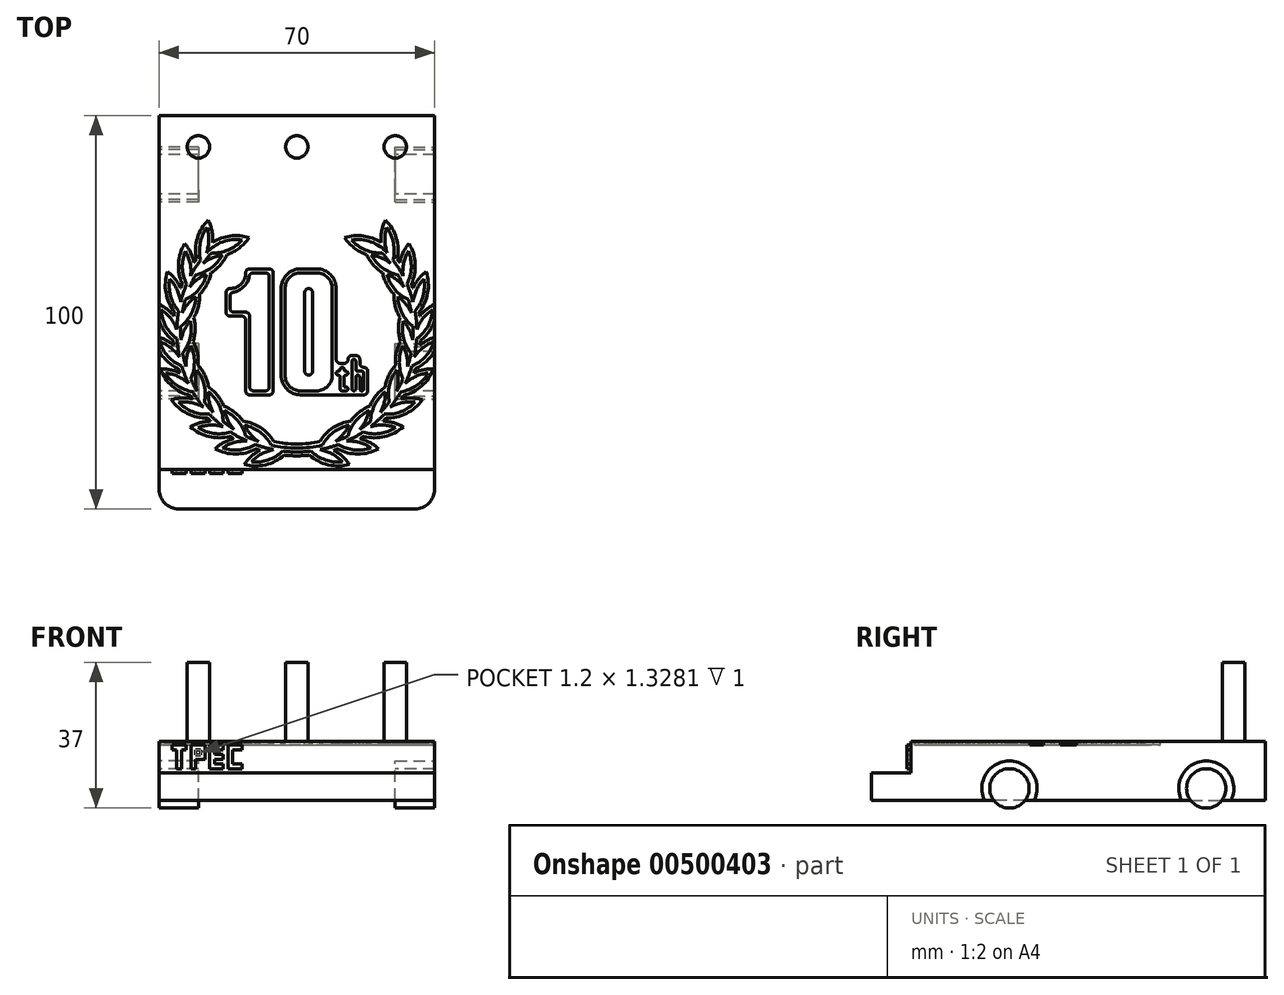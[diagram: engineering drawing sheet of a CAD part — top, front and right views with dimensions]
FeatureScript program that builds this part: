
annotation { "Feature Type Name" : "Feature", "Feature Type Description" : "" }
export const myFeature = defineFeature(function(context is Context, id is Id, definition is map)
    precondition{}
    {
        {
            var Q0;
            Q0=qCreatedBy(makeId("Top.planeOp"),FACE);
            var sketch = newSketch(context, id + "F0", { "sketchPlane" : qUnion([Q0])});
            skLineSegment(sketch, "E0.bottom", {"start": v(35, -50) * mm, "end": v(-35, -50) * mm});
            skLineSegment(sketch, "E0.top", {"start": v(35, 50) * mm, "end": v(-35, 50) * mm});
            skLineSegment(sketch, "E0.left", {"start": v(35, -50) * mm, "end": v(35, 50) * mm});
            skLineSegment(sketch, "E0.right", {"start": v(-35, -50) * mm, "end": v(-35, 50) * mm});
            skPoint(sketch, "E0.middle", {"position": v(0, 0) * mm});
            skSolve(sketch);
        }
        {
            var Q0;
            Q0 = qSketchRegion(id + "F0", true);
            extrude(context, id + "F1", {"entities" : qUnion([Q0]), "depth" : 15 * mm});
        }
        {
            var Q0;
            Q0=makeQuery(id+"F1.opExtrude","CAP_FACE",FACE,{"disambiguationData":[OSD([sQuery(id+"F0.wireOp",EDGE,"E0.bottom"),sQuery(id+"F0.wireOp",EDGE,"E0.top"),sQuery(id+"F0.wireOp",EDGE,"E0.left"),sQuery(id+"F0.wireOp",EDGE,"E0.right")])],"isStart":false});
            var sketch = newSketch(context, id + "F2", { "sketchPlane" : qUnion([Q0])});
            skLineSegment(sketch, "E1.bottom", {"start": v(35, -50) * mm, "end": v(-35, -50) * mm});
            skLineSegment(sketch, "E1.top", {"start": v(35, -40) * mm, "end": v(-35, -40) * mm});
            skLineSegment(sketch, "E1.left", {"start": v(35, -50) * mm, "end": v(35, -40) * mm});
            skLineSegment(sketch, "E1.right", {"start": v(-35, -50) * mm, "end": v(-35, -40) * mm});
            skSolve(sketch);
        }
        {
            var Q0;
            Q0 = qSketchRegion(id + "F2", true);
            extrude(context, id + "F3", {"entities" : qUnion([Q0]), "operationType" : NewBodyOperationType.REMOVE, "oppositeDirection" : true, "depth" : 8 * mm});
        }
        {
            var Q0;
            Q0=makeQuery(id+"F1.opExtrude","CAP_FACE",FACE,{"disambiguationData":[OSD([sQuery(id+"F0.wireOp",EDGE,"E0.bottom"),sQuery(id+"F0.wireOp",EDGE,"E0.top"),sQuery(id+"F0.wireOp",EDGE,"E0.left"),sQuery(id+"F0.wireOp",EDGE,"E0.right")])],"isStart":false});
            var sketch = newSketch(context, id + "F4", { "sketchPlane" : qUnion([Q0])});
            skLineSegment(sketch, "E2", {"start": v(-65.6, 42) * mm, "end": v(65.6, 42) * mm, "construction": true});
            skLineSegment(sketch, "E3", {"start": v(0, 50) * mm, "end": v(0, -40) * mm, "construction": true});
            skCircle(sketch, "E4", {"center": v(0, 42) * mm, "radius": 2.85 * mm});
            skCircle(sketch, "E5", {"center": v(-25, 42) * mm, "radius": 2.85 * mm});
            skCircle(sketch, "E6.MirrorC", {"center": v(25, 42) * mm, "radius": 2.85 * mm});
            skSolve(sketch);
        }
        {
            var Q0;
            Q0 = qSketchRegion(id + "F4", true);
            extrude(context, id + "F5", {"entities" : qUnion([Q0]), "operationType" : NewBodyOperationType.ADD, "depth" : 20 * mm});
        }
        {
            var Q0;
            Q0=makeQuery(id+"F1.opExtrude","SWEPT_FACE",FACE,{"disambiguationData":[OSD([sQuery(id+"F0.wireOp",EDGE,"E0.left")])]});
            var sketch = newSketch(context, id + "F6", { "sketchPlane" : qUnion([Q0])});
            skLineSegment(sketch, "E7", {"start": v(-57.55, -2) * mm, "end": v(59.86, -2) * mm, "construction": true});
            skLineSegment(sketch, "E8", {"start": v(-15, 24.29) * mm, "end": v(-15, -23.36) * mm, "construction": true});
            skLineSegment(sketch, "E9", {"start": v(35, 23.38) * mm, "end": v(35, -24.94) * mm, "construction": true});
            skPoint(sketch, "E10", {"position": v(-15, -2) * mm});
            skPoint(sketch, "E11", {"position": v(35, -2) * mm});
            skLineSegment(sketch, "E12", {"start": v(-54.96, 3) * mm, "end": v(63.1, 3) * mm, "construction": true});
            skPoint(sketch, "E13", {"position": v(-15, 3) * mm});
            skPoint(sketch, "E14", {"position": v(35, 3) * mm});
            skCircle(sketch, "E15", {"center": v(-15, 3) * mm, "radius": 5 * mm, "construction": true});
            skCircle(sketch, "E16", {"center": v(35, 3) * mm, "radius": 5 * mm, "construction": true});
            skLineSegment(sketch, "E17.bottom", {"start": v(-21, 0) * mm, "end": v(-9, 0) * mm});
            skLineSegment(sketch, "E17.top", {"start": v(-21, 9) * mm, "end": v(-9, 9) * mm});
            skLineSegment(sketch, "E17.left", {"start": v(-21, 0) * mm, "end": v(-21, 9) * mm});
            skLineSegment(sketch, "E17.right", {"start": v(-9, 0) * mm, "end": v(-9, 9) * mm});
            skLineSegment(sketch, "E18.bottom", {"start": v(29, 0) * mm, "end": v(41, 0) * mm});
            skLineSegment(sketch, "E18.top", {"start": v(29, 9) * mm, "end": v(41, 9) * mm});
            skLineSegment(sketch, "E18.left", {"start": v(29, 0) * mm, "end": v(29, 9) * mm});
            skLineSegment(sketch, "E18.right", {"start": v(41, 0) * mm, "end": v(41, 9) * mm});
            skPoint(sketch, "E19", {"position": v(-15, 9) * mm});
            skPoint(sketch, "E20", {"position": v(35, 9) * mm});
            skSolve(sketch);
        }
        {
            var Q0;
            Q0=qCreatedBy(makeId("Right.planeOp"),FACE);
            var sketch = newSketch(context, id + "F7", { "sketchPlane" : qUnion([Q0])});
            skLineSegment(sketch, "E21.0", {"start": v(-54.96, 3) * mm, "end": v(63.1, 3) * mm, "construction": true});
            skPoint(sketch, "E22.0", {"position": v(-15, 3) * mm});
            skPoint(sketch, "E23.0", {"position": v(35, 3) * mm});
            skCircle(sketch, "E24.0", {"center": v(-15, 3) * mm, "radius": 5 * mm});
            skCircle(sketch, "E24.1", {"center": v(35, 3) * mm, "radius": 5 * mm});
            skSolve(sketch);
        }
        {
            var Q0;
            Q0 = qSketchRegion(id + "F7", true);
            var Q1;
            Q1=makeQuery(id+"F1.opExtrude","SWEPT_FACE",FACE,{"disambiguationData":[OSD([sQuery(id+"F0.wireOp",EDGE,"E0.left")])]});
            var Q2;
            Q2=makeQuery(id+"F1.opExtrude","SWEPT_FACE",FACE,{"disambiguationData":[OSD([sQuery(id+"F0.wireOp",EDGE,"E0.right")])]});
            extrude(context, id + "F8", {"entities" : qUnion([Q0]), "operationType" : NewBodyOperationType.ADD, "endBound" : BoundingType.UP_TO_SURFACE, "endBoundEntityFace" : qUnion([Q1]), "depth" : 25 * mm, "hasSecondDirection" : true, "secondDirectionBound" : SecondDirectionBoundingType.UP_TO_SURFACE, "secondDirectionOppositeDirection" : true, "secondDirectionBoundEntityFace" : qUnion([Q2]), "secondDirectionDepth" : 25 * mm});
        }
        {
            var Q0;
            Q0=qCreatedBy(makeId("Right.planeOp"),FACE);
            var sketch = newSketch(context, id + "F9", { "sketchPlane" : qUnion([Q0])});
            skArc(sketch, "E25.0", {"start": v(-19, 0) * mm, "mid": v(-15, -2) * mm, "end": v(-11, 0) * mm});
            skArc(sketch, "E26.0", {"start": v(31, 0) * mm, "mid": v(35, -2) * mm, "end": v(39, 0) * mm});
            skLineSegment(sketch, "E27.0", {"start": v(-11, 0) * mm, "end": v(31, 0) * mm, "construction": true});
            skLineSegment(sketch, "E28", {"start": v(-11, 0) * mm, "end": v(-19, 0) * mm});
            skLineSegment(sketch, "E29", {"start": v(31, 0) * mm, "end": v(39, 0) * mm});
            skSolve(sketch);
        }
        {
            var Q0;
            Q0 = qSketchRegion(id + "F9", true);
            extrude(context, id + "F10", {"entities" : qUnion([Q0]), "operationType" : NewBodyOperationType.REMOVE, "oppositeDirection" : true, "depth" : 25 * mm, "hasSecondDirection" : true, "secondDirectionOppositeDirection" : false, "secondDirectionDepth" : 25 * mm});
        }
        {
            var Q0;
            Q0=makeQuery(id+"F6.imprint","IMPRINT",FACE,{"disambiguationData":[TD([[makeQuery(id+"F6.imprint","IMPRINT",EDGE,{"derivedFrom":sQuery(id+"F6.wireOp",EDGE,"E17.top")}),1.0]])]});
            var sketch = newSketch(context, id + "F11", { "sketchPlane" : qUnion([Q0])});
            skCircle(sketch, "E30.0", {"center": v(-15, 3) * mm, "radius": 5 * mm});
            skCircle(sketch, "E31.0", {"center": v(-15, 3) * mm, "radius": 7 * mm});
            skCircle(sketch, "E32.0", {"center": v(35, 3) * mm, "radius": 5 * mm});
            skCircle(sketch, "E33.0", {"center": v(35, 3) * mm, "radius": 7 * mm});
            skSolve(sketch);
        }
        {
            var Q0;
            Q0 = qSketchRegion(id + "F11", true);
            extrude(context, id + "F12", {"entities" : qUnion([Q0]), "operationType" : NewBodyOperationType.REMOVE, "oppositeDirection" : true, "depth" : 10 * mm});
        }
        {
            var Q0;
            Q0=makeQuery(id+"F8.boolean.opBoolean","MERGE",FACE,{"derivedFrom":[makeQuery(id+"F1.opExtrude","SWEPT_FACE",FACE,{"disambiguationData":[OSD([sQuery(id+"F0.wireOp",EDGE,"E0.right")])]}),makeQuery(id+"F8.opExtrude","CAP_FACE",FACE,{"disambiguationData":[OSD([sQuery(id+"F7.wireOp",EDGE,"E24.0")])],"isStart":true}),makeQuery(id+"F8.opExtrude","CAP_FACE",FACE,{"disambiguationData":[OSD([sQuery(id+"F7.wireOp",EDGE,"E24.1")])],"isStart":true})]});
            var sketch = newSketch(context, id + "F13", { "sketchPlane" : qUnion([Q0])});
            skCircle(sketch, "E34.0", {"center": v(15, 3) * mm, "radius": 5 * mm});
            skCircle(sketch, "E34.1", {"center": v(-35, 3) * mm, "radius": 5 * mm});
            skCircle(sketch, "E35.0", {"center": v(15, 3) * mm, "radius": 7 * mm});
            skCircle(sketch, "E36.0", {"center": v(-35, 3) * mm, "radius": 7 * mm});
            skSolve(sketch);
        }
        {
            var Q0;
            Q0 = qSketchRegion(id + "F13", true);
            extrude(context, id + "F14", {"entities" : qUnion([Q0]), "operationType" : NewBodyOperationType.REMOVE, "oppositeDirection" : true, "depth" : 10 * mm});
        }
        {
            var Q0;
            Q0=makeQuery(id+"F1.opExtrude","SWEPT_EDGE",EDGE,{"disambiguationData":[OSD([sQuery(id+"F0.wireOp",EDGE,"E0.bottom"),sQuery(id+"F0.wireOp",EDGE,"E0.left")])]});
            var Q1;
            Q1=makeQuery(id+"F1.opExtrude","SWEPT_EDGE",EDGE,{"disambiguationData":[OSD([sQuery(id+"F0.wireOp",EDGE,"E0.bottom"),sQuery(id+"F0.wireOp",EDGE,"E0.right")])]});
            fillet(context, id + "F15", {"entities" : qUnion([Q0, Q1]), "radius" : 5 * mm, "tangentPropagation" : true, "allowEdgeOverflow" : false});
        }
        {
            var Q0;
            Q0=makeQuery(id+"F3.boolean.opBoolean","COPY",FACE,{"derivedFrom":makeQuery(id+"F3.opExtrude","SWEPT_FACE",FACE,{"disambiguationData":[OSD([sQuery(id+"F2.wireOp",EDGE,"E1.top")])]})});
            var sketch = newSketch(context, id + "F16", { "sketchPlane" : qUnion([Q0])});
            skLineSegment(sketch, "E37", {"start": v(-31.71, 14) * mm, "end": v(-28.11, 14) * mm});
            skLineSegment(sketch, "E38", {"start": v(-28.11, 14) * mm, "end": v(-28.11, 12.8) * mm});
            skLineSegment(sketch, "E39", {"start": v(-28.11, 12.8) * mm, "end": v(-29.31, 12.8) * mm});
            skLineSegment(sketch, "E40", {"start": v(-29.31, 12.8) * mm, "end": v(-29.31, 8) * mm});
            skLineSegment(sketch, "E41", {"start": v(-29.31, 8) * mm, "end": v(-30.51, 8) * mm});
            skLineSegment(sketch, "E42", {"start": v(-30.51, 8) * mm, "end": v(-30.51, 12.8) * mm});
            skLineSegment(sketch, "E43", {"start": v(-30.51, 12.8) * mm, "end": v(-31.71, 12.8) * mm});
            skLineSegment(sketch, "E44", {"start": v(-31.71, 12.8) * mm, "end": v(-31.71, 14) * mm});
            skLineSegment(sketch, "E45", {"start": v(-26.91, 14) * mm, "end": v(-26.91, 8) * mm});
            skLineSegment(sketch, "E46", {"start": v(-26.91, 8) * mm, "end": v(-25.71, 8) * mm});
            skLineSegment(sketch, "E47", {"start": v(-25.71, 8) * mm, "end": v(-25.71, 10.4) * mm});
            skLineSegment(sketch, "E48", {"start": v(-25.71, 10.4) * mm, "end": v(-23.31, 10.4) * mm});
            skLineSegment(sketch, "E49", {"start": v(-23.31, 10.4) * mm, "end": v(-23.31, 14) * mm});
            skLineSegment(sketch, "E50", {"start": v(-23.31, 14) * mm, "end": v(-26.91, 14) * mm});
            skLineSegment(sketch, "E51", {"start": v(-22.11, 14) * mm, "end": v(-22.11, 8) * mm});
            skLineSegment(sketch, "E52", {"start": v(-22.11, 8) * mm, "end": v(-18.67, 8) * mm});
            skLineSegment(sketch, "E53", {"start": v(-18.67, 8) * mm, "end": v(-18.67, 9.2) * mm});
            skLineSegment(sketch, "E54", {"start": v(-18.67, 9.2) * mm, "end": v(-20.91, 9.2) * mm});
            skLineSegment(sketch, "E55", {"start": v(-20.91, 9.2) * mm, "end": v(-20.91, 10.4) * mm});
            skLineSegment(sketch, "E56", {"start": v(-20.91, 10.4) * mm, "end": v(-18.67, 10.4) * mm});
            skLineSegment(sketch, "E57", {"start": v(-18.67, 10.4) * mm, "end": v(-18.67, 11.6) * mm});
            skLineSegment(sketch, "E58", {"start": v(-18.67, 11.6) * mm, "end": v(-20.91, 11.6) * mm});
            skLineSegment(sketch, "E59", {"start": v(-20.91, 11.6) * mm, "end": v(-20.91, 12.8) * mm});
            skLineSegment(sketch, "E60", {"start": v(-20.91, 12.8) * mm, "end": v(-18.67, 12.8) * mm});
            skLineSegment(sketch, "E61", {"start": v(-18.67, 12.8) * mm, "end": v(-18.67, 14) * mm});
            skLineSegment(sketch, "E62", {"start": v(-18.67, 14) * mm, "end": v(-22.11, 14) * mm});
            skLineSegment(sketch, "E63", {"start": v(-13.87, 14) * mm, "end": v(-17.47, 14) * mm});
            skLineSegment(sketch, "E64", {"start": v(-17.47, 14) * mm, "end": v(-17.47, 8) * mm});
            skLineSegment(sketch, "E65", {"start": v(-17.47, 8) * mm, "end": v(-13.87, 8) * mm});
            skLineSegment(sketch, "E66", {"start": v(-13.87, 8) * mm, "end": v(-13.87, 9.2) * mm});
            skLineSegment(sketch, "E67", {"start": v(-13.87, 9.2) * mm, "end": v(-16.27, 9.2) * mm});
            skLineSegment(sketch, "E68", {"start": v(-13.87, 14) * mm, "end": v(-13.87, 12.8) * mm});
            skLineSegment(sketch, "E69", {"start": v(-13.87, 12.8) * mm, "end": v(-16.27, 12.8) * mm});
            skLineSegment(sketch, "E70", {"start": v(-16.27, 12.8) * mm, "end": v(-16.27, 9.2) * mm});
            skLineSegment(sketch, "E71.bottom", {"start": v(-25.71, 11.47) * mm, "end": v(-24.51, 11.47) * mm});
            skLineSegment(sketch, "E71.top", {"start": v(-25.71, 12.8) * mm, "end": v(-24.51, 12.8) * mm});
            skLineSegment(sketch, "E71.left", {"start": v(-25.71, 11.47) * mm, "end": v(-25.71, 12.8) * mm});
            skLineSegment(sketch, "E71.right", {"start": v(-24.51, 11.47) * mm, "end": v(-24.51, 12.8) * mm});
            skSolve(sketch);
        }
        {
            var Q0;
            Q0 = qSketchRegion(id + "F16", true);
            extrude(context, id + "F17", {"entities" : qUnion([Q0]), "operationType" : NewBodyOperationType.ADD, "depth" : 1 * mm});
        }
        {
            var Q0;
            Q0=makeQuery(id+"F1.opExtrude","CAP_FACE",FACE,{"disambiguationData":[OSD([sQuery(id+"F0.wireOp",EDGE,"E0.bottom"),sQuery(id+"F0.wireOp",EDGE,"E0.top"),sQuery(id+"F0.wireOp",EDGE,"E0.left"),sQuery(id+"F0.wireOp",EDGE,"E0.right")])],"isStart":false});
            var sketch = newSketch(context, id + "F18", { "sketchPlane" : qUnion([Q0])});
            skLineSegment(sketch, "E72", {"start": v(-35, 30) * mm, "end": v(35, 30) * mm, "construction": true});
            skLineSegment(sketch, "E73", {"start": v(35, 30) * mm, "end": v(35, -40) * mm, "construction": true});
            skLineSegment(sketch, "E74", {"start": v(35, -40) * mm, "end": v(-35, -40) * mm, "construction": true});
            skLineSegment(sketch, "E75", {"start": v(-35, -40) * mm, "end": v(-35, 30) * mm, "construction": true});
            skCircle(sketch, "E76", {"center": v(0, -5) * mm, "radius": 30 * mm, "construction": true});
            skArc(sketch, "E77.0", {"start": v(5.88, -34.93) * mm, "mid": v(8.2, -34.38) * mm, "end": v(10.47, -33.65) * mm});
            skArc(sketch, "E78.0", {"start": v(9.78, -32.83) * mm, "mid": v(11.4, -32.2) * mm, "end": v(12.98, -31.5) * mm});
            skPoint(sketch, "E79.startSnap0", {"position": v(0, 50) * mm});
            skPoint(sketch, "E79.endSnap0", {"position": v(0, -40) * mm});
            skLineSegment(sketch, "E80", {"start": v(0, -5) * mm, "end": v(3.14, -34.84) * mm, "construction": true});
            skLineSegment(sketch, "E81", {"start": v(0, -5) * mm, "end": v(0, -25.77) * mm, "construction": true});
            skArc(sketch, "E82", {"start": v(11.55, -38.02) * mm, "mid": v(8.98, -36) * mm, "end": v(5.88, -34.93) * mm});
            skLineSegment(sketch, "E83", {"start": v(3.14, -34.84) * mm, "end": v(11.55, -38.02) * mm, "construction": true});
            skArc(sketch, "E84.MirrorCS", {"start": v(11.55, -38.02) * mm, "mid": v(7.26, -37.54) * mm, "end": v(3.58, -35.29) * mm});
            skLineSegment(sketch, "E85", {"start": v(0, -5) * mm, "end": v(6.24, -34.34) * mm, "construction": true});
            skArc(sketch, "E86", {"start": v(13.26, -28.71) * mm, "mid": v(9.33, -30.5) * mm, "end": v(6.52, -33.77) * mm});
            skLineSegment(sketch, "E87", {"start": v(13.26, -28.71) * mm, "end": v(6.24, -34.34) * mm, "construction": true});
            skArc(sketch, "E88.MirrorCS", {"start": v(13.26, -28.71) * mm, "mid": v(11.8, -31) * mm, "end": v(9.78, -32.83) * mm});
            skPoint(sketch, "E89.orphan", {"position": v(6.24, -34.34) * mm});
            skPoint(sketch, "E90.orphan", {"position": v(3.14, -34.84) * mm});
            skArc(sketch, "E91.1.0", {"start": v(18.37, -25.02) * mm, "mid": v(14.96, -27.66) * mm, "end": v(12.98, -31.5) * mm});
            skArc(sketch, "E91.1.1", {"start": v(18.37, -25.02) * mm, "mid": v(17.48, -27.59) * mm, "end": v(15.94, -29.82) * mm});
            skArc(sketch, "E91.1.2", {"start": v(18.86, -34.47) * mm, "mid": v(15.88, -33.1) * mm, "end": v(12.63, -32.76) * mm});
            skArc(sketch, "E91.1.3", {"start": v(18.86, -34.47) * mm, "mid": v(14.57, -34.99) * mm, "end": v(10.47, -33.65) * mm});
            skArc(sketch, "E91.2.0", {"start": v(22.49, -20.24) * mm, "mid": v(19.78, -23.6) * mm, "end": v(18.74, -27.78) * mm});
            skArc(sketch, "E91.2.1", {"start": v(22.49, -20.24) * mm, "mid": v(22.22, -22.95) * mm, "end": v(21.23, -25.48) * mm});
            skArc(sketch, "E91.2.2", {"start": v(25.14, -29.33) * mm, "mid": v(21.94, -28.68) * mm, "end": v(18.69, -29.1) * mm});
            skArc(sketch, "E91.2.3", {"start": v(25.14, -29.33) * mm, "mid": v(21.1, -30.82) * mm, "end": v(16.8, -30.46) * mm});
            skArc(sketch, "E91.3.0", {"start": v(25.4, -14.64) * mm, "mid": v(23.54, -18.53) * mm, "end": v(23.49, -22.85) * mm});
            skArc(sketch, "E91.3.1", {"start": v(25.4, -14.64) * mm, "mid": v(25.76, -17.34) * mm, "end": v(25.38, -20.03) * mm});
            skArc(sketch, "E91.3.2", {"start": v(30.08, -22.87) * mm, "mid": v(26.8, -22.98) * mm, "end": v(23.74, -24.14) * mm});
            skArc(sketch, "E91.3.3", {"start": v(30.08, -22.87) * mm, "mid": v(26.48, -25.26) * mm, "end": v(22.21, -25.9) * mm});
            skArc(sketch, "E91.4.0", {"start": v(26.94, -8.53) * mm, "mid": v(26.02, -12.74) * mm, "end": v(26.97, -16.95) * mm});
            skArc(sketch, "E91.4.1", {"start": v(26.94, -8.53) * mm, "mid": v(27.91, -11.06) * mm, "end": v(28.17, -13.77) * mm});
            skArc(sketch, "E91.4.2", {"start": v(33.39, -15.45) * mm, "mid": v(30.23, -16.32) * mm, "end": v(27.52, -18.15) * mm});
            skArc(sketch, "E91.4.3", {"start": v(33.39, -15.45) * mm, "mid": v(30.44, -18.6) * mm, "end": v(26.43, -20.22) * mm});
            skArc(sketch, "E91.5.0", {"start": v(27.02, -2.22) * mm, "mid": v(27.1, -6.53) * mm, "end": v(29, -10.4) * mm});
            skArc(sketch, "E91.5.1", {"start": v(27.02, -2.22) * mm, "mid": v(28.56, -4.46) * mm, "end": v(29.43, -7.04) * mm});
            skArc(sketch, "E91.5.2", {"start": v(34.9, -7.47) * mm, "mid": v(32.02, -9.04) * mm, "end": v(29.81, -11.45) * mm});
            skArc(sketch, "E91.5.3", {"start": v(34.9, -7.47) * mm, "mid": v(32.75, -11.22) * mm, "end": v(29.23, -13.71) * mm});
            skArc(sketch, "E91.6.0", {"start": v(25.65, 3.94) * mm, "mid": v(26.73, -0.24) * mm, "end": v(29.47, -3.57) * mm});
            skArc(sketch, "E91.6.1", {"start": v(25.65, 3.94) * mm, "mid": v(27.66, 2.1) * mm, "end": v(29.1, -0.2) * mm});
            skArc(sketch, "E91.6.2", {"start": v(34.53, 0.64) * mm, "mid": v(32.1, -1.55) * mm, "end": v(30.5, -4.4) * mm});
            skArc(sketch, "E91.6.3", {"start": v(34.53, 0.64) * mm, "mid": v(33.3, -3.5) * mm, "end": v(30.45, -6.74) * mm});
            skArc(sketch, "E91.7.0", {"start": v(22.9, 9.61) * mm, "mid": v(24.91, 5.8) * mm, "end": v(28.34, 3.18) * mm});
            skArc(sketch, "E91.7.1", {"start": v(22.9, 9.61) * mm, "mid": v(25.28, 8.3) * mm, "end": v(27.21, 6.39) * mm});
            skArc(sketch, "E91.7.2", {"start": v(32.3, 8.45) * mm, "mid": v(30.43, 5.76) * mm, "end": v(29.53, 2.61) * mm});
            skArc(sketch, "E91.7.3", {"start": v(32.3, 8.45) * mm, "mid": v(32.06, 4.14) * mm, "end": v(30.03, 0.33) * mm});
            skArc(sketch, "E91.8.0", {"start": v(18.91, 14.5) * mm, "mid": v(21.75, 11.25) * mm, "end": v(25.7, 9.5) * mm});
            skArc(sketch, "E91.8.1", {"start": v(18.91, 14.5) * mm, "mid": v(21.53, 13.77) * mm, "end": v(23.85, 12.36) * mm});
            skArc(sketch, "E91.8.2", {"start": v(28.32, 15.54) * mm, "mid": v(27.13, 12.5) * mm, "end": v(26.98, 9.22) * mm});
            skArc(sketch, "E91.8.3", {"start": v(28.32, 15.54) * mm, "mid": v(29.09, 11.3) * mm, "end": v(28, 7.12) * mm});
            skArc(sketch, "E91.9.0", {"start": v(13.9, 18.34) * mm, "mid": v(17.42, 15.83) * mm, "end": v(21.65, 15.03) * mm});
            skArc(sketch, "E91.9.3", {"start": v(22.82, 21.52) * mm, "mid": v(24.55, 17.56) * mm, "end": v(24.44, 13.24) * mm});
            skLineSegment(sketch, "E91.anchor1", {"start": v(0, -5) * mm, "end": v(4.18, -44.78) * mm, "construction": true});
            skLineSegment(sketch, "E91.anchor2", {"start": v(0, -5) * mm, "end": v(32.36, 18.51) * mm, "construction": true});
            skArc(sketch, "E92.trimOffspring", {"start": v(12.63, -32.76) * mm, "mid": v(14.75, -31.7) * mm, "end": v(16.8, -30.46) * mm});
            skArc(sketch, "E93.trimOffspring", {"start": v(15.94, -29.82) * mm, "mid": v(17.37, -28.84) * mm, "end": v(18.74, -27.78) * mm});
            skArc(sketch, "E94.trimOffspring", {"start": v(18.69, -29.1) * mm, "mid": v(20.51, -27.57) * mm, "end": v(22.21, -25.9) * mm});
            skArc(sketch, "E95.trimOffspring", {"start": v(21.23, -25.48) * mm, "mid": v(22.4, -24.2) * mm, "end": v(23.49, -22.85) * mm});
            skArc(sketch, "E96.trimOffspring", {"start": v(23.74, -24.14) * mm, "mid": v(25.17, -22.23) * mm, "end": v(26.43, -20.22) * mm});
            skArc(sketch, "E97.trimOffspring", {"start": v(25.38, -20.03) * mm, "mid": v(26.22, -18.51) * mm, "end": v(26.97, -16.95) * mm});
            skArc(sketch, "E98.trimOffspring", {"start": v(27.52, -18.15) * mm, "mid": v(28.46, -15.96) * mm, "end": v(29.23, -13.71) * mm});
            skArc(sketch, "E99.trimOffspring", {"start": v(28.17, -13.77) * mm, "mid": v(28.63, -12.1) * mm, "end": v(29, -10.4) * mm});
            skArc(sketch, "E100.trimOffspring", {"start": v(29.81, -11.45) * mm, "mid": v(30.22, -9.1) * mm, "end": v(30.45, -6.74) * mm});
            skArc(sketch, "E101.trimOffspring", {"start": v(29.43, -7.04) * mm, "mid": v(29.5, -5.3) * mm, "end": v(29.47, -3.57) * mm});
            skArc(sketch, "E102.trimOffspring", {"start": v(30.5, -4.4) * mm, "mid": v(30.35, -2.02) * mm, "end": v(30.03, 0.33) * mm});
            skArc(sketch, "E103.trimOffspring", {"start": v(29.1, -0.2) * mm, "mid": v(28.77, 1.5) * mm, "end": v(28.34, 3.18) * mm});
            skArc(sketch, "E104.trimOffspring", {"start": v(29.53, 2.61) * mm, "mid": v(28.85, 4.9) * mm, "end": v(28, 7.12) * mm});
            skArc(sketch, "E105.trimOffspring", {"start": v(23.87, 12.34) * mm, "mid": v(22.8, 13.72) * mm, "end": v(21.65, 15.03) * mm});
            skArc(sketch, "E106.trimOffspring", {"start": v(26.98, 9.22) * mm, "mid": v(25.8, 11.28) * mm, "end": v(24.44, 13.24) * mm});
            skArc(sketch, "E107.trimOffspring", {"start": v(-24.44, 13.24) * mm, "mid": v(-25.8, 11.28) * mm, "end": v(-26.98, 9.22) * mm});
            skArc(sketch, "E108", {"start": v(25.7, 9.5) * mm, "mid": v(26.5, 7.97) * mm, "end": v(27.21, 6.39) * mm});
            skLineSegment(sketch, "E109", {"start": v(0, -5) * mm, "end": v(24.27, 12.63) * mm, "construction": true});
            skArc(sketch, "E110", {"start": v(22.82, 21.52) * mm, "mid": v(22.36, 18.28) * mm, "end": v(22.98, 15.06) * mm});
            skArc(sketch, "E111", {"start": v(22.98, 15.06) * mm, "mid": v(18.86, 17.86) * mm, "end": v(13.9, 18.34) * mm});
            skArc(sketch, "E112.trimOffspring", {"start": v(-21.65, 15.03) * mm, "mid": v(-22.8, 13.73) * mm, "end": v(-23.85, 12.36) * mm});
            skArc(sketch, "E113.MirrorCS", {"start": v(-22.82, 21.52) * mm, "mid": v(-24.55, 17.56) * mm, "end": v(-24.44, 13.24) * mm});
            skArc(sketch, "E114.MirrorCS", {"start": v(-22.82, 21.52) * mm, "mid": v(-22.36, 18.28) * mm, "end": v(-22.98, 15.06) * mm});
            skArc(sketch, "E115.MirrorCS", {"start": v(-22.98, 15.06) * mm, "mid": v(-18.86, 17.86) * mm, "end": v(-13.9, 18.34) * mm});
            skArc(sketch, "E116.MirrorCS", {"start": v(-13.9, 18.34) * mm, "mid": v(-17.42, 15.83) * mm, "end": v(-21.65, 15.03) * mm});
            skArc(sketch, "E117.MirrorCS", {"start": v(-18.91, 14.5) * mm, "mid": v(-21.53, 13.77) * mm, "end": v(-23.85, 12.36) * mm});
            skArc(sketch, "E118.MirrorCS", {"start": v(-18.91, 14.5) * mm, "mid": v(-21.75, 11.25) * mm, "end": v(-25.7, 9.5) * mm});
            skArc(sketch, "E119.MirrorCS", {"start": v(-28.32, 15.54) * mm, "mid": v(-27.13, 12.5) * mm, "end": v(-26.98, 9.22) * mm});
            skArc(sketch, "E120.MirrorCS", {"start": v(-28.32, 15.54) * mm, "mid": v(-29.09, 11.3) * mm, "end": v(-28, 7.12) * mm});
            skArc(sketch, "E121.MirrorCS", {"start": v(-22.9, 9.61) * mm, "mid": v(-25.28, 8.3) * mm, "end": v(-27.21, 6.39) * mm});
            skArc(sketch, "E122.MirrorCS", {"start": v(-22.9, 9.61) * mm, "mid": v(-24.91, 5.8) * mm, "end": v(-28.34, 3.18) * mm});
            skArc(sketch, "E123.MirrorCS", {"start": v(-32.3, 8.45) * mm, "mid": v(-30.43, 5.76) * mm, "end": v(-29.53, 2.61) * mm});
            skArc(sketch, "E124.MirrorCS", {"start": v(-32.3, 8.45) * mm, "mid": v(-32.06, 4.14) * mm, "end": v(-30.03, 0.33) * mm});
            skArc(sketch, "E125.MirrorCS", {"start": v(-25.65, 3.94) * mm, "mid": v(-27.66, 2.1) * mm, "end": v(-29.1, -0.2) * mm});
            skArc(sketch, "E126.MirrorCS", {"start": v(-25.65, 3.94) * mm, "mid": v(-26.73, -0.24) * mm, "end": v(-29.47, -3.57) * mm});
            skArc(sketch, "E127.MirrorCS", {"start": v(-34.53, 0.64) * mm, "mid": v(-32.1, -1.55) * mm, "end": v(-30.5, -4.4) * mm});
            skArc(sketch, "E128.MirrorCS", {"start": v(-34.53, 0.64) * mm, "mid": v(-33.3, -3.5) * mm, "end": v(-30.45, -6.74) * mm});
            skArc(sketch, "E129.MirrorCS", {"start": v(-27.02, -2.22) * mm, "mid": v(-28.56, -4.46) * mm, "end": v(-29.43, -7.04) * mm});
            skArc(sketch, "E130.MirrorCS", {"start": v(-27.02, -2.22) * mm, "mid": v(-27.1, -6.53) * mm, "end": v(-29, -10.4) * mm});
            skArc(sketch, "E131.MirrorCS", {"start": v(-34.9, -7.47) * mm, "mid": v(-32.75, -11.22) * mm, "end": v(-29.23, -13.71) * mm});
            skArc(sketch, "E132.MirrorCS", {"start": v(-34.9, -7.47) * mm, "mid": v(-32.02, -9.04) * mm, "end": v(-29.81, -11.45) * mm});
            skArc(sketch, "E133.MirrorCS", {"start": v(-26.94, -8.53) * mm, "mid": v(-27.91, -11.06) * mm, "end": v(-28.17, -13.77) * mm});
            skArc(sketch, "E134.MirrorCS", {"start": v(-26.94, -8.53) * mm, "mid": v(-26.02, -12.74) * mm, "end": v(-26.97, -16.95) * mm});
            skArc(sketch, "E135.MirrorCS", {"start": v(-25.4, -14.64) * mm, "mid": v(-25.76, -17.34) * mm, "end": v(-25.38, -20.03) * mm});
            skArc(sketch, "E136.MirrorCS", {"start": v(-33.39, -15.45) * mm, "mid": v(-30.44, -18.6) * mm, "end": v(-26.43, -20.22) * mm});
            skArc(sketch, "E137.MirrorCS", {"start": v(-33.39, -15.45) * mm, "mid": v(-30.23, -16.32) * mm, "end": v(-27.52, -18.15) * mm});
            skArc(sketch, "E138.MirrorCS", {"start": v(-25.4, -14.64) * mm, "mid": v(-23.54, -18.53) * mm, "end": v(-23.49, -22.85) * mm});
            skArc(sketch, "E139.MirrorCS", {"start": v(-30.08, -22.87) * mm, "mid": v(-26.8, -22.98) * mm, "end": v(-23.74, -24.14) * mm});
            skArc(sketch, "E140.MirrorCS", {"start": v(-25.14, -29.33) * mm, "mid": v(-21.1, -30.82) * mm, "end": v(-16.8, -30.46) * mm});
            skArc(sketch, "E141.MirrorCS", {"start": v(-25.14, -29.33) * mm, "mid": v(-21.94, -28.68) * mm, "end": v(-18.69, -29.1) * mm});
            skArc(sketch, "E142.MirrorCS", {"start": v(-30.08, -22.87) * mm, "mid": v(-26.48, -25.26) * mm, "end": v(-22.21, -25.9) * mm});
            skArc(sketch, "E143.MirrorCS", {"start": v(-22.49, -20.24) * mm, "mid": v(-22.22, -22.95) * mm, "end": v(-21.23, -25.48) * mm});
            skArc(sketch, "E144.MirrorCS", {"start": v(-22.49, -20.24) * mm, "mid": v(-19.78, -23.6) * mm, "end": v(-18.74, -27.78) * mm});
            skArc(sketch, "E145.MirrorCS", {"start": v(-11.55, -38.02) * mm, "mid": v(-7.26, -37.54) * mm, "end": v(-3.58, -35.29) * mm});
            skArc(sketch, "E146.MirrorCS", {"start": v(-11.55, -38.02) * mm, "mid": v(-8.98, -36) * mm, "end": v(-5.88, -34.93) * mm});
            skArc(sketch, "E147.MirrorCS", {"start": v(-18.86, -34.47) * mm, "mid": v(-14.57, -34.99) * mm, "end": v(-10.47, -33.65) * mm});
            skArc(sketch, "E148.MirrorCS", {"start": v(-18.86, -34.47) * mm, "mid": v(-15.88, -33.1) * mm, "end": v(-12.63, -32.76) * mm});
            skArc(sketch, "E149.MirrorCS", {"start": v(-18.37, -25.02) * mm, "mid": v(-17.48, -27.59) * mm, "end": v(-15.94, -29.82) * mm});
            skArc(sketch, "E150.MirrorCS", {"start": v(-18.37, -25.02) * mm, "mid": v(-14.96, -27.66) * mm, "end": v(-12.98, -31.5) * mm});
            skArc(sketch, "E151.MirrorCS", {"start": v(-13.26, -28.71) * mm, "mid": v(-11.8, -31) * mm, "end": v(-9.78, -32.83) * mm});
            skArc(sketch, "E152.MirrorCS", {"start": v(-13.26, -28.71) * mm, "mid": v(-9.33, -30.5) * mm, "end": v(-6.52, -33.77) * mm});
            skArc(sketch, "E153.trimOffspring", {"start": v(-25.7, 9.5) * mm, "mid": v(-26.5, 7.97) * mm, "end": v(-27.21, 6.39) * mm});
            skArc(sketch, "E154.trimOffspring", {"start": v(-28, 7.12) * mm, "mid": v(-28.85, 4.9) * mm, "end": v(-29.53, 2.61) * mm});
            skArc(sketch, "E155.trimOffspring", {"start": v(-28.34, 3.18) * mm, "mid": v(-28.77, 1.5) * mm, "end": v(-29.1, -0.2) * mm});
            skArc(sketch, "E156.trimOffspring", {"start": v(-30.03, 0.33) * mm, "mid": v(-30.35, -2.02) * mm, "end": v(-30.5, -4.4) * mm});
            skArc(sketch, "E157.trimOffspring", {"start": v(-29.47, -3.57) * mm, "mid": v(-29.5, -5.3) * mm, "end": v(-29.43, -7.04) * mm});
            skArc(sketch, "E158.trimOffspring", {"start": v(-30.45, -6.74) * mm, "mid": v(-30.22, -9.1) * mm, "end": v(-29.81, -11.45) * mm});
            skArc(sketch, "E159.trimOffspring", {"start": v(-29, -10.4) * mm, "mid": v(-28.63, -12.1) * mm, "end": v(-28.17, -13.77) * mm});
            skArc(sketch, "E160.trimOffspring", {"start": v(-29.23, -13.71) * mm, "mid": v(-28.46, -15.96) * mm, "end": v(-27.52, -18.15) * mm});
            skArc(sketch, "E161.trimOffspring", {"start": v(-26.97, -16.95) * mm, "mid": v(-26.22, -18.51) * mm, "end": v(-25.38, -20.03) * mm});
            skArc(sketch, "E162.trimOffspring", {"start": v(-26.43, -20.22) * mm, "mid": v(-25.17, -22.23) * mm, "end": v(-23.74, -24.14) * mm});
            skArc(sketch, "E163.trimOffspring", {"start": v(-23.49, -22.85) * mm, "mid": v(-22.4, -24.2) * mm, "end": v(-21.23, -25.48) * mm});
            skArc(sketch, "E164.trimOffspring", {"start": v(-22.21, -25.9) * mm, "mid": v(-20.51, -27.57) * mm, "end": v(-18.69, -29.1) * mm});
            skArc(sketch, "E165.trimOffspring", {"start": v(-18.74, -27.78) * mm, "mid": v(-17.37, -28.84) * mm, "end": v(-15.94, -29.82) * mm});
            skArc(sketch, "E166.trimOffspring", {"start": v(-16.8, -30.46) * mm, "mid": v(-14.75, -31.7) * mm, "end": v(-12.63, -32.76) * mm});
            skArc(sketch, "E167.trimOffspring", {"start": v(-12.98, -31.5) * mm, "mid": v(-11.4, -32.2) * mm, "end": v(-9.78, -32.83) * mm});
            skArc(sketch, "E168.trimOffspring", {"start": v(-10.47, -33.65) * mm, "mid": v(-8.2, -34.38) * mm, "end": v(-5.88, -34.93) * mm});
            skArc(sketch, "E169.trimOffspring", {"start": v(-6.52, -33.77) * mm, "mid": v(0, -34.5) * mm, "end": v(6.52, -33.77) * mm});
            skArc(sketch, "E170.trimOffspring", {"start": v(-3.58, -35.29) * mm, "mid": v(0, -35.5) * mm, "end": v(3.58, -35.29) * mm});
            skArc(sketch, "E171.0", {"start": v(12.17, 18.95) * mm, "mid": v(14.6, 16.34) * mm, "end": v(17.72, 14.64) * mm});
            skArc(sketch, "E172.0", {"start": v(17.72, 14.64) * mm, "mid": v(19.42, 12.04) * mm, "end": v(21.77, 10.02) * mm});
            skArc(sketch, "E173.0", {"start": v(24.65, 4.6) * mm, "mid": v(25, 1.51) * mm, "end": v(26.2, -1.35) * mm});
            skArc(sketch, "E174.0", {"start": v(26.2, -1.35) * mm, "mid": v(25.83, -4.43) * mm, "end": v(26.34, -7.49) * mm});
            skArc(sketch, "E175.0", {"start": v(26.34, -7.49) * mm, "mid": v(25.27, -10.4) * mm, "end": v(25.05, -13.5) * mm});
            skArc(sketch, "E176.0", {"start": v(25.05, -13.5) * mm, "mid": v(23.34, -16.08) * mm, "end": v(22.42, -19.04) * mm});
            skArc(sketch, "E177.0", {"start": v(22.42, -19.04) * mm, "mid": v(20.16, -21.17) * mm, "end": v(18.58, -23.84) * mm});
            skArc(sketch, "E178.0", {"start": v(18.58, -23.84) * mm, "mid": v(15.88, -25.38) * mm, "end": v(13.73, -27.61) * mm});
            skArc(sketch, "E179.0", {"start": v(13.73, -27.61) * mm, "mid": v(9.2, -29.36) * mm, "end": v(5.87, -32.89) * mm});
            skArc(sketch, "E180.0", {"start": v(-6.3, -32.8) * mm, "mid": v(-0.22, -33.5) * mm, "end": v(5.87, -32.89) * mm});
            skArc(sketch, "E181.0", {"start": v(21.77, 10.02) * mm, "mid": v(22.83, 7.1) * mm, "end": v(24.65, 4.6) * mm});
            skArc(sketch, "E182.0", {"start": v(22.51, 23.41) * mm, "mid": v(21.57, 20.65) * mm, "end": v(21.39, 17.73) * mm});
            skArc(sketch, "E183.trimOffspring", {"start": v(21.39, 17.73) * mm, "mid": v(16.91, 19.36) * mm, "end": v(12.17, 18.95) * mm});
            skArc(sketch, "E184.0", {"start": v(22.51, 23.41) * mm, "mid": v(25.26, 18.82) * mm, "end": v(25.52, 13.47) * mm});
            skArc(sketch, "E185.0", {"start": v(28.46, 17.46) * mm, "mid": v(27, 15.17) * mm, "end": v(26.13, 12.6) * mm});
            skArc(sketch, "E186.0", {"start": v(28.46, 17.46) * mm, "mid": v(30.07, 12.35) * mm, "end": v(29.09, 7.09) * mm});
            skArc(sketch, "E187.0", {"start": v(29.48, 6.1) * mm, "mid": v(29.29, 6.6) * mm, "end": v(29.09, 7.09) * mm});
            skArc(sketch, "E188.0", {"start": v(32.87, 10.29) * mm, "mid": v(30.92, 8.4) * mm, "end": v(29.48, 6.1) * mm});
            skArc(sketch, "E189.0", {"start": v(32.87, 10.29) * mm, "mid": v(33.27, 4.95) * mm, "end": v(31.1, 0.05) * mm});
            skArc(sketch, "E190.trimOffspring", {"start": v(26.13, 12.6) * mm, "mid": v(25.81, 13.06) * mm, "end": v(25.48, 13.52) * mm});
            skArc(sketch, "E191.0", {"start": v(35, 2.06) * mm, "mid": v(32.95, 0.74) * mm, "end": v(31.25, -1) * mm});
            skArc(sketch, "E192.0", {"start": v(35, -2.1) * mm, "mid": v(33.58, -4.94) * mm, "end": v(31.42, -7.25) * mm});
            skArc(sketch, "E193.0", {"start": v(35, -6.39) * mm, "mid": v(33.07, -7.18) * mm, "end": v(31.32, -8.32) * mm});
            skArc(sketch, "E194.0", {"start": v(35, -9.78) * mm, "mid": v(32.9, -12.5) * mm, "end": v(30.05, -14.44) * mm});
            skArc(sketch, "E195.0", {"start": v(35, -14.42) * mm, "mid": v(32.3, -14.6) * mm, "end": v(29.72, -15.45) * mm});
            skArc(sketch, "E196.0", {"start": v(35, -14.42) * mm, "mid": v(31.88, -18.76) * mm, "end": v(27.07, -21.11) * mm});
            skArc(sketch, "E197.0", {"start": v(26.5, -22.02) * mm, "mid": v(26.79, -21.57) * mm, "end": v(27.07, -21.11) * mm});
            skArc(sketch, "E198.0", {"start": v(31.9, -22.24) * mm, "mid": v(29.21, -21.8) * mm, "end": v(26.5, -22.02) * mm});
            skArc(sketch, "E199.0", {"start": v(31.9, -22.24) * mm, "mid": v(27.84, -25.74) * mm, "end": v(22.62, -26.92) * mm});
            skArc(sketch, "E200.0", {"start": v(21.86, -27.68) * mm, "mid": v(22.25, -27.3) * mm, "end": v(22.62, -26.92) * mm});
            skArc(sketch, "E201.0", {"start": v(27.06, -29.13) * mm, "mid": v(24.55, -28.08) * mm, "end": v(21.86, -27.68) * mm});
            skArc(sketch, "E202.0", {"start": v(27.06, -29.13) * mm, "mid": v(22.3, -31.6) * mm, "end": v(16.96, -31.55) * mm});
            skArc(sketch, "E203.trimOffspring", {"start": v(31.25, -1) * mm, "mid": v(31.17, -0.47) * mm, "end": v(31.1, 0.05) * mm});
            skArc(sketch, "E204.trimOffspring", {"start": v(31.32, -8.32) * mm, "mid": v(31.38, -7.79) * mm, "end": v(31.42, -7.25) * mm});
            skArc(sketch, "E205.trimOffspring", {"start": v(29.72, -15.45) * mm, "mid": v(29.89, -14.95) * mm, "end": v(30.05, -14.44) * mm});
            skArc(sketch, "E206.0", {"start": v(20.76, -34.72) * mm, "mid": v(18.57, -33.12) * mm, "end": v(16.05, -32.1) * mm});
            skArc(sketch, "E207.0", {"start": v(20.76, -34.72) * mm, "mid": v(15.57, -36.03) * mm, "end": v(10.38, -34.74) * mm});
            skArc(sketch, "E208.0", {"start": v(9.36, -35.08) * mm, "mid": v(9.87, -34.91) * mm, "end": v(10.38, -34.74) * mm});
            skArc(sketch, "E209.0", {"start": v(13.35, -38.7) * mm, "mid": v(8, -38.79) * mm, "end": v(3.24, -36.33) * mm});
            skArc(sketch, "E210.0", {"start": v(-3.7, -36.28) * mm, "mid": v(-0.23, -36.5) * mm, "end": v(3.24, -36.33) * mm});
            skArc(sketch, "E211.trimOffspring", {"start": v(16.05, -32.1) * mm, "mid": v(16.5, -31.83) * mm, "end": v(16.96, -31.55) * mm});
            skArc(sketch, "E212.0", {"start": v(13.35, -38.7) * mm, "mid": v(11.58, -36.64) * mm, "end": v(9.36, -35.08) * mm});
            skArc(sketch, "E213.MirrorCS", {"start": v(-22.51, 23.41) * mm, "mid": v(-21.57, 20.65) * mm, "end": v(-21.39, 17.73) * mm});
            skArc(sketch, "E214.MirrorCS", {"start": v(-22.51, 23.41) * mm, "mid": v(-25.26, 18.82) * mm, "end": v(-25.52, 13.47) * mm});
            skArc(sketch, "E215.MirrorCS", {"start": v(-28.46, 17.46) * mm, "mid": v(-27, 15.17) * mm, "end": v(-26.13, 12.6) * mm});
            skArc(sketch, "E216.MirrorCS", {"start": v(-26.13, 12.6) * mm, "mid": v(-25.81, 13.06) * mm, "end": v(-25.48, 13.52) * mm});
            skArc(sketch, "E217.MirrorCS", {"start": v(-28.46, 17.46) * mm, "mid": v(-30.07, 12.35) * mm, "end": v(-29.09, 7.09) * mm});
            skArc(sketch, "E218.MirrorCS", {"start": v(-32.87, 10.29) * mm, "mid": v(-30.92, 8.4) * mm, "end": v(-29.48, 6.1) * mm});
            skArc(sketch, "E219.MirrorCS", {"start": v(-29.48, 6.1) * mm, "mid": v(-29.29, 6.6) * mm, "end": v(-29.09, 7.09) * mm});
            skArc(sketch, "E220.MirrorCS", {"start": v(-32.87, 10.29) * mm, "mid": v(-33.27, 4.95) * mm, "end": v(-31.1, 0.05) * mm});
            skArc(sketch, "E221.MirrorCS", {"start": v(-31.25, -1) * mm, "mid": v(-31.17, -0.47) * mm, "end": v(-31.1, 0.05) * mm});
            skArc(sketch, "E222.MirrorCS", {"start": v(-35, 2.06) * mm, "mid": v(-32.95, 0.74) * mm, "end": v(-31.25, -1) * mm});
            skArc(sketch, "E223.MirrorCS", {"start": v(-35, -6.39) * mm, "mid": v(-33.07, -7.18) * mm, "end": v(-31.32, -8.32) * mm});
            skArc(sketch, "E224.MirrorCS", {"start": v(-35, -2.1) * mm, "mid": v(-33.58, -4.94) * mm, "end": v(-31.42, -7.25) * mm});
            skArc(sketch, "E225.MirrorCS", {"start": v(-31.32, -8.32) * mm, "mid": v(-31.38, -7.79) * mm, "end": v(-31.42, -7.25) * mm});
            skArc(sketch, "E226.MirrorCS", {"start": v(-35, -14.42) * mm, "mid": v(-32.3, -14.6) * mm, "end": v(-29.72, -15.45) * mm});
            skArc(sketch, "E227.MirrorCS", {"start": v(-35, -9.78) * mm, "mid": v(-32.9, -12.5) * mm, "end": v(-30.05, -14.44) * mm});
            skArc(sketch, "E228.MirrorCS", {"start": v(-29.72, -15.45) * mm, "mid": v(-29.89, -14.95) * mm, "end": v(-30.05, -14.44) * mm});
            skArc(sketch, "E229.MirrorCS", {"start": v(-31.9, -22.24) * mm, "mid": v(-29.21, -21.8) * mm, "end": v(-26.5, -22.02) * mm});
            skArc(sketch, "E230.MirrorCS", {"start": v(-35, -14.42) * mm, "mid": v(-31.88, -18.76) * mm, "end": v(-27.07, -21.11) * mm});
            skArc(sketch, "E231.MirrorCS", {"start": v(-26.5, -22.02) * mm, "mid": v(-26.79, -21.57) * mm, "end": v(-27.07, -21.11) * mm});
            skArc(sketch, "E232.MirrorCS", {"start": v(-31.9, -22.24) * mm, "mid": v(-27.84, -25.74) * mm, "end": v(-22.62, -26.92) * mm});
            skArc(sketch, "E233.MirrorCS", {"start": v(-27.06, -29.13) * mm, "mid": v(-24.55, -28.08) * mm, "end": v(-21.86, -27.68) * mm});
            skArc(sketch, "E234.MirrorCS", {"start": v(-21.86, -27.68) * mm, "mid": v(-22.25, -27.3) * mm, "end": v(-22.62, -26.92) * mm});
            skArc(sketch, "E235.MirrorCS", {"start": v(-27.06, -29.13) * mm, "mid": v(-22.3, -31.6) * mm, "end": v(-16.96, -31.55) * mm});
            skArc(sketch, "E236.MirrorCS", {"start": v(-20.76, -34.72) * mm, "mid": v(-18.57, -33.12) * mm, "end": v(-16.05, -32.1) * mm});
            skArc(sketch, "E237.MirrorCS", {"start": v(-16.05, -32.1) * mm, "mid": v(-16.5, -31.83) * mm, "end": v(-16.96, -31.55) * mm});
            skArc(sketch, "E238.MirrorCS", {"start": v(-20.76, -34.72) * mm, "mid": v(-15.57, -36.03) * mm, "end": v(-10.38, -34.74) * mm});
            skArc(sketch, "E239.MirrorCS", {"start": v(-9.36, -35.08) * mm, "mid": v(-9.87, -34.91) * mm, "end": v(-10.38, -34.74) * mm});
            skArc(sketch, "E240.MirrorCS", {"start": v(-13.35, -38.7) * mm, "mid": v(-11.58, -36.64) * mm, "end": v(-9.36, -35.08) * mm});
            skArc(sketch, "E241.MirrorCS", {"start": v(-13.35, -38.7) * mm, "mid": v(-8, -38.79) * mm, "end": v(-3.24, -36.33) * mm});
            skArc(sketch, "E242.MirrorCS", {"start": v(-13.73, -27.61) * mm, "mid": v(-9.2, -29.36) * mm, "end": v(-5.87, -32.89) * mm});
            skArc(sketch, "E243.MirrorCS", {"start": v(-18.58, -23.84) * mm, "mid": v(-15.88, -25.38) * mm, "end": v(-13.73, -27.61) * mm});
            skArc(sketch, "E244.MirrorCS", {"start": v(-22.42, -19.04) * mm, "mid": v(-20.16, -21.17) * mm, "end": v(-18.58, -23.84) * mm});
            skArc(sketch, "E245.MirrorCS", {"start": v(-25.05, -13.5) * mm, "mid": v(-23.34, -16.08) * mm, "end": v(-22.42, -19.04) * mm});
            skArc(sketch, "E246.MirrorCS", {"start": v(-26.34, -7.49) * mm, "mid": v(-25.27, -10.4) * mm, "end": v(-25.05, -13.5) * mm});
            skArc(sketch, "E247.MirrorCS", {"start": v(-26.2, -1.35) * mm, "mid": v(-25.83, -4.43) * mm, "end": v(-26.34, -7.49) * mm});
            skArc(sketch, "E248.MirrorCS", {"start": v(-24.65, 4.6) * mm, "mid": v(-25, 1.51) * mm, "end": v(-26.2, -1.35) * mm});
            skArc(sketch, "E249.MirrorCS", {"start": v(-21.77, 10.02) * mm, "mid": v(-22.83, 7.1) * mm, "end": v(-24.65, 4.6) * mm});
            skArc(sketch, "E250.MirrorCS", {"start": v(-17.72, 14.64) * mm, "mid": v(-19.42, 12.04) * mm, "end": v(-21.77, 10.02) * mm});
            skArc(sketch, "E251.MirrorCS", {"start": v(-12.17, 18.95) * mm, "mid": v(-14.6, 16.34) * mm, "end": v(-17.72, 14.64) * mm});
            skArc(sketch, "E252.MirrorCS", {"start": v(-21.39, 17.73) * mm, "mid": v(-16.91, 19.36) * mm, "end": v(-12.17, 18.95) * mm});
            skLineSegment(sketch, "E253", {"start": v(35, 2.06) * mm, "end": v(35, -2.1) * mm});
            skLineSegment(sketch, "E254", {"start": v(35, -6.39) * mm, "end": v(35, -9.78) * mm});
            skLineSegment(sketch, "E255", {"start": v(-35, 2.06) * mm, "end": v(-35, -2.1) * mm});
            skLineSegment(sketch, "E256", {"start": v(-35, -6.39) * mm, "end": v(-35, -9.78) * mm});
            skSolve(sketch);
        }
        {
            var Q0;
            Q0 = qSketchRegion(id + "F18", true);
            extrude(context, id + "F19", {"entities" : qUnion([Q0]), "operationType" : NewBodyOperationType.REMOVE, "oppositeDirection" : true, "depth" : 1 * mm});
        }
        {
            var Q0;
            {var subQ1=sQuery(id+"F0.wireOp",EDGE,"E0.right");var subQ2=sQuery(id+"F0.wireOp",EDGE,"E0.left");var subQ3=sQuery(id+"F0.wireOp",EDGE,"E0.top");Q0=makeQuery(id+"F19.boolean.opBoolean","SPLIT",FACE,{"disambiguationData":[TD([makeQuery(id+"F1.opExtrude","SWEPT_FACE",FACE,{"disambiguationData":[OSD([subQ3])]})])],"derivedFrom":makeQuery(id+"F1.opExtrude","CAP_FACE",FACE,{"disambiguationData":[OSD([sQuery(id+"F0.wireOp",EDGE,"E0.bottom"),subQ3,subQ2,subQ1])],"isStart":false})});}
            var sketch = newSketch(context, id + "F20", { "sketchPlane" : qUnion([Q0])});
            skLineSegment(sketch, "E257", {"start": v(-56.5, -5) * mm, "end": v(59.53, -5) * mm, "construction": true});
            skLineSegment(sketch, "E258", {"start": v(0, 25.1) * mm, "end": v(0, -54.33) * mm, "construction": true});
            skPoint(sketch, "E259", {"position": v(0, -5) * mm});
            skCircle(sketch, "E260", {"center": v(0, -5) * mm, "radius": 30 * mm, "construction": true});
            skLineSegment(sketch, "E261", {"start": v(-12, 10) * mm, "end": v(-7, 10) * mm});
            skLineSegment(sketch, "E262", {"start": v(-7, 10) * mm, "end": v(-7, -20) * mm});
            skLineSegment(sketch, "E263", {"start": v(-7, -20) * mm, "end": v(-12, -20) * mm});
            skLineSegment(sketch, "E264", {"start": v(-12, -20) * mm, "end": v(-12, 0) * mm});
            skLineSegment(sketch, "E265", {"start": v(-12, 0) * mm, "end": v(-17, 0) * mm});
            skLineSegment(sketch, "E266", {"start": v(-17, 0) * mm, "end": v(-17, 5) * mm});
            skLineSegment(sketch, "E267.bottom", {"start": v(1, 10) * mm, "end": v(5, 10) * mm});
            skLineSegment(sketch, "E267.top", {"start": v(1, -20) * mm, "end": v(5, -20) * mm});
            skLineSegment(sketch, "E267.left", {"start": v(-3, 6) * mm, "end": v(-3, -16) * mm});
            skLineSegment(sketch, "E267.right", {"start": v(9, 6) * mm, "end": v(9, -16) * mm});
            skPoint(sketch, "E268", {"position": v(9, -5) * mm});
            skArc(sketch, "E269", {"start": v(-17, 5) * mm, "mid": v(-13.46, 6.46) * mm, "end": v(-12, 10) * mm});
            skPoint(sketch, "E270.visualSharp", {"position": v(-3, 10) * mm});
            skArc(sketch, "E270.filletArc", {"start": v(1, 10) * mm, "mid": v(-1.83, 8.83) * mm, "end": v(-3, 6) * mm});
            skLineSegment(sketch, "E271.0", {"start": v(-6, 11) * mm, "end": v(-6, -21) * mm});
            skLineSegment(sketch, "E272.0", {"start": v(-14.02, 11) * mm, "end": v(-6, 11) * mm});
            skArc(sketch, "E273.0", {"start": v(-17, 6) * mm, "mid": v(-14.17, 7.17) * mm, "end": v(-13, 10) * mm});
            skLineSegment(sketch, "E274.0", {"start": v(-18, -1) * mm, "end": v(-18, 5) * mm});
            skLineSegment(sketch, "E275.0", {"start": v(-13, -1) * mm, "end": v(-18, -1) * mm});
            skLineSegment(sketch, "E276.0", {"start": v(-13, -21) * mm, "end": v(-13, -1) * mm});
            skLineSegment(sketch, "E277.0", {"start": v(-6, -21) * mm, "end": v(-13, -21) * mm});
            skLineSegment(sketch, "E278", {"start": v(-13, 10) * mm, "end": v(-13, 11) * mm});
            skLineSegment(sketch, "E279", {"start": v(-17, 6) * mm, "end": v(-18, 6) * mm});
            skLineSegment(sketch, "E280", {"start": v(-14.02, 11) * mm, "end": v(-13, 11) * mm});
            skLineSegment(sketch, "E281", {"start": v(-18, 6) * mm, "end": v(-18, 5) * mm});
            skPoint(sketch, "E282.visualSharp", {"position": v(9, 10) * mm});
            skArc(sketch, "E282.filletArc", {"start": v(9, 6) * mm, "mid": v(7.83, 8.83) * mm, "end": v(5, 10) * mm});
            skPoint(sketch, "E283.visualSharp", {"position": v(-3, -20) * mm});
            skArc(sketch, "E283.filletArc", {"start": v(-3, -16) * mm, "mid": v(-1.83, -18.83) * mm, "end": v(1, -20) * mm});
            skPoint(sketch, "E284.visualSharp", {"position": v(9, -20) * mm});
            skArc(sketch, "E284.filletArc", {"start": v(5, -20) * mm, "mid": v(7.83, -18.83) * mm, "end": v(9, -16) * mm});
            skArc(sketch, "E285.0", {"start": v(1, 11) * mm, "mid": v(-2.54, 9.54) * mm, "end": v(-4, 6) * mm});
            skLineSegment(sketch, "E286.0", {"start": v(1, 11) * mm, "end": v(5, 11) * mm});
            skArc(sketch, "E287.0", {"start": v(10, 6) * mm, "mid": v(8.54, 9.54) * mm, "end": v(5, 11) * mm});
            skLineSegment(sketch, "E288.0", {"start": v(-4, 6) * mm, "end": v(-4, -16) * mm});
            skArc(sketch, "E289.0", {"start": v(-4, -16) * mm, "mid": v(-2.54, -19.54) * mm, "end": v(1, -21) * mm});
            skLineSegment(sketch, "E290.0", {"start": v(1, -21) * mm, "end": v(5, -21) * mm});
            skLineSegment(sketch, "E291.0", {"start": v(10, 6) * mm, "end": v(10, -13) * mm});
            skLineSegment(sketch, "E292", {"start": v(3, 14.53) * mm, "end": v(3, -28.16) * mm, "construction": true});
            skPoint(sketch, "E293", {"position": v(3, 11) * mm});
            skLineSegment(sketch, "E294.bottom", {"start": v(3, 6) * mm, "end": v(3, 6) * mm});
            skLineSegment(sketch, "E294.top", {"start": v(3, -16) * mm, "end": v(3, -16) * mm});
            skLineSegment(sketch, "E294.left", {"start": v(2, 5) * mm, "end": v(2, -15) * mm});
            skLineSegment(sketch, "E294.right", {"start": v(4, 5) * mm, "end": v(4, -15) * mm});
            skPoint(sketch, "E295", {"position": v(4, -5) * mm});
            skPoint(sketch, "E296", {"position": v(3, 6) * mm});
            skPoint(sketch, "E297.visualSharp", {"position": v(2, 6) * mm});
            skArc(sketch, "E297.filletArc", {"start": v(3, 6) * mm, "mid": v(2.3, 5.7) * mm, "end": v(2, 5) * mm});
            skPoint(sketch, "E298.visualSharp", {"position": v(4, 6) * mm});
            skArc(sketch, "E298.filletArc", {"start": v(4, 5) * mm, "mid": v(3.7, 5.7) * mm, "end": v(3, 6) * mm});
            skPoint(sketch, "E299.visualSharp", {"position": v(2, -16) * mm});
            skArc(sketch, "E299.filletArc", {"start": v(2, -15) * mm, "mid": v(2.3, -15.7) * mm, "end": v(3, -16) * mm});
            skPoint(sketch, "E300.visualSharp", {"position": v(4, -16) * mm});
            skArc(sketch, "E300.filletArc", {"start": v(3, -16) * mm, "mid": v(3.7, -15.7) * mm, "end": v(4, -15) * mm});
            skLineSegment(sketch, "E301.bottom", {"start": v(11, -14) * mm, "end": v(12, -14) * mm});
            skLineSegment(sketch, "E301.top", {"start": v(11, -20) * mm, "end": v(12, -20) * mm});
            skLineSegment(sketch, "E301.left", {"start": v(11, -14) * mm, "end": v(11, -15) * mm});
            skLineSegment(sketch, "E301.right", {"start": v(12, -14) * mm, "end": v(12, -15) * mm});
            skLineSegment(sketch, "E302.bottom", {"start": v(10, -15) * mm, "end": v(11, -15) * mm});
            skLineSegment(sketch, "E302.top", {"start": v(10, -16) * mm, "end": v(11, -16) * mm});
            skLineSegment(sketch, "E302.left", {"start": v(10, -15) * mm, "end": v(10, -16) * mm});
            skLineSegment(sketch, "E302.right", {"start": v(13, -15) * mm, "end": v(13, -16) * mm});
            skLineSegment(sketch, "E303.trimOffspring", {"start": v(11, -16) * mm, "end": v(11, -20) * mm});
            skLineSegment(sketch, "E304.trimOffspring", {"start": v(12, -15) * mm, "end": v(13, -15) * mm});
            skLineSegment(sketch, "E305.trimOffspring", {"start": v(12, -16) * mm, "end": v(13, -16) * mm});
            skLineSegment(sketch, "E306.trimOffspring", {"start": v(12, -16) * mm, "end": v(12, -19) * mm});
            skLineSegment(sketch, "E307", {"start": v(10, -13) * mm, "end": v(13, -13) * mm});
            skLineSegment(sketch, "E308", {"start": v(14, -14) * mm, "end": v(14, -17) * mm});
            skLineSegment(sketch, "E309", {"start": v(18, -21) * mm, "end": v(10, -21) * mm});
            skPoint(sketch, "E310.endSnap0", {"position": v(11.5, -14) * mm});
            skLineSegment(sketch, "E311", {"start": v(13, -11) * mm, "end": v(16, -11) * mm});
            skLineSegment(sketch, "E312", {"start": v(18, -21) * mm, "end": v(18, -14) * mm});
            skPoint(sketch, "E312.endSnap0", {"position": v(13.5, -14) * mm});
            skLineSegment(sketch, "E313", {"start": v(18, -14) * mm, "end": v(16, -14) * mm});
            skLineSegment(sketch, "E314", {"start": v(16, -14) * mm, "end": v(16, -11) * mm});
            skLineSegment(sketch, "E315", {"start": v(14, -12) * mm, "end": v(14, -20) * mm});
            skLineSegment(sketch, "E316", {"start": v(14, -20) * mm, "end": v(15, -20) * mm});
            skLineSegment(sketch, "E317", {"start": v(15, -20) * mm, "end": v(15, -16) * mm});
            skLineSegment(sketch, "E318", {"start": v(14, -12) * mm, "end": v(15, -12) * mm});
            skLineSegment(sketch, "E319", {"start": v(15, -12) * mm, "end": v(15, -15) * mm});
            skLineSegment(sketch, "E320", {"start": v(15, -15) * mm, "end": v(17, -15) * mm});
            skLineSegment(sketch, "E321", {"start": v(17, -15) * mm, "end": v(17, -20) * mm});
            skLineSegment(sketch, "E322", {"start": v(17, -20) * mm, "end": v(16, -20) * mm});
            skLineSegment(sketch, "E323", {"start": v(16, -20) * mm, "end": v(16, -16) * mm});
            skLineSegment(sketch, "E324", {"start": v(16, -16) * mm, "end": v(15, -16) * mm});
            skLineSegment(sketch, "E325.trimOffspring", {"start": v(13, -16) * mm, "end": v(13, -15) * mm});
            skPoint(sketch, "E326.end.orphan", {"position": v(13, -17) * mm});
            skLineSegment(sketch, "E327.trimOffspring", {"start": v(13, -13) * mm, "end": v(13, -11) * mm});
            skPoint(sketch, "E328.start.orphan", {"position": v(13, -14) * mm});
            skLineSegment(sketch, "E329", {"start": v(18, -21) * mm, "end": v(-19.76, -21) * mm, "construction": true});
            skPoint(sketch, "E310.end.orphan", {"position": v(9, -14) * mm});
            skPoint(sketch, "E330.orphan", {"position": v(10, -14) * mm});
            skLineSegment(sketch, "E331", {"start": v(12, -20) * mm, "end": v(13, -20) * mm});
            skLineSegment(sketch, "E332", {"start": v(13, -20) * mm, "end": v(13, -19) * mm});
            skLineSegment(sketch, "E333", {"start": v(13, -19) * mm, "end": v(12, -19) * mm});
            skPoint(sketch, "E334.start.orphan", {"position": v(10, -17) * mm});
            skLineSegment(sketch, "E335", {"start": v(5, -21) * mm, "end": v(10, -21) * mm});
            skSolve(sketch);
        }
        {
            var Q0;
            Q0 = qSketchRegion(id + "F20", true);
            var Q1;
            Q1=makeQuery(id+"F20.imprint","IMPRINT",FACE,{"disambiguationData":[TD([[makeQuery(id+"F20.imprint","IMPRINT",EDGE,{"derivedFrom":sQuery(id+"F20.wireOp",EDGE,"E294.left")}),1.0]])]});
            extrude(context, id + "F21", {"entities" : qUnion([Q0, Q1]), "operationType" : NewBodyOperationType.REMOVE, "oppositeDirection" : true, "depth" : 1 * mm});
        }
        {
            var Q0;
            Q0=makeQuery(id+"F19.boolean.opBoolean","COPY",FACE,{"derivedFrom":makeQuery(id+"F19.opExtrude","CAP_FACE",FACE,{"disambiguationData":[OSD([sQuery(id+"F18.wireOp",EDGE,"E77.0"),sQuery(id+"F18.wireOp",EDGE,"E78.0"),sQuery(id+"F18.wireOp",EDGE,"E82"),sQuery(id+"F18.wireOp",EDGE,"E84.MirrorCS"),sQuery(id+"F18.wireOp",EDGE,"E86"),sQuery(id+"F18.wireOp",EDGE,"E88.MirrorCS"),sQuery(id+"F18.wireOp",EDGE,"E91.1.0"),sQuery(id+"F18.wireOp",EDGE,"E91.1.1"),sQuery(id+"F18.wireOp",EDGE,"E91.1.2"),sQuery(id+"F18.wireOp",EDGE,"E91.1.3"),sQuery(id+"F18.wireOp",EDGE,"E91.2.0"),sQuery(id+"F18.wireOp",EDGE,"E91.2.1"),sQuery(id+"F18.wireOp",EDGE,"E91.2.2"),sQuery(id+"F18.wireOp",EDGE,"E91.2.3"),sQuery(id+"F18.wireOp",EDGE,"E91.3.0"),sQuery(id+"F18.wireOp",EDGE,"E91.3.1"),sQuery(id+"F18.wireOp",EDGE,"E91.3.2"),sQuery(id+"F18.wireOp",EDGE,"E91.3.3"),sQuery(id+"F18.wireOp",EDGE,"E91.4.0"),sQuery(id+"F18.wireOp",EDGE,"E91.4.1"),sQuery(id+"F18.wireOp",EDGE,"E91.4.2"),sQuery(id+"F18.wireOp",EDGE,"E91.4.3"),sQuery(id+"F18.wireOp",EDGE,"E91.5.0"),sQuery(id+"F18.wireOp",EDGE,"E91.5.1"),sQuery(id+"F18.wireOp",EDGE,"E91.5.2"),sQuery(id+"F18.wireOp",EDGE,"E91.5.3"),sQuery(id+"F18.wireOp",EDGE,"E91.6.0"),sQuery(id+"F18.wireOp",EDGE,"E91.6.1"),sQuery(id+"F18.wireOp",EDGE,"E91.6.2"),sQuery(id+"F18.wireOp",EDGE,"E91.6.3"),sQuery(id+"F18.wireOp",EDGE,"E91.7.0"),sQuery(id+"F18.wireOp",EDGE,"E91.7.1"),sQuery(id+"F18.wireOp",EDGE,"E91.7.2"),sQuery(id+"F18.wireOp",EDGE,"E91.7.3"),sQuery(id+"F18.wireOp",EDGE,"E91.8.0"),sQuery(id+"F18.wireOp",EDGE,"E91.8.1"),sQuery(id+"F18.wireOp",EDGE,"E91.8.2"),sQuery(id+"F18.wireOp",EDGE,"E91.8.3"),sQuery(id+"F18.wireOp",EDGE,"E91.9.0"),sQuery(id+"F18.wireOp",EDGE,"E91.9.3"),sQuery(id+"F18.wireOp",EDGE,"E92.trimOffspring"),sQuery(id+"F18.wireOp",EDGE,"E93.trimOffspring"),sQuery(id+"F18.wireOp",EDGE,"E94.trimOffspring"),sQuery(id+"F18.wireOp",EDGE,"E95.trimOffspring"),sQuery(id+"F18.wireOp",EDGE,"E96.trimOffspring"),sQuery(id+"F18.wireOp",EDGE,"E97.trimOffspring"),sQuery(id+"F18.wireOp",EDGE,"E98.trimOffspring"),sQuery(id+"F18.wireOp",EDGE,"E99.trimOffspring"),sQuery(id+"F18.wireOp",EDGE,"E100.trimOffspring"),sQuery(id+"F18.wireOp",EDGE,"E101.trimOffspring"),sQuery(id+"F18.wireOp",EDGE,"E102.trimOffspring"),sQuery(id+"F18.wireOp",EDGE,"E103.trimOffspring"),sQuery(id+"F18.wireOp",EDGE,"E104.trimOffspring"),sQuery(id+"F18.wireOp",EDGE,"E105.trimOffspring"),sQuery(id+"F18.wireOp",EDGE,"E106.trimOffspring"),sQuery(id+"F18.wireOp",EDGE,"E107.trimOffspring"),sQuery(id+"F18.wireOp",EDGE,"E108"),sQuery(id+"F18.wireOp",EDGE,"E110"),sQuery(id+"F18.wireOp",EDGE,"E111"),sQuery(id+"F18.wireOp",EDGE,"E112.trimOffspring"),sQuery(id+"F18.wireOp",EDGE,"E113.MirrorCS"),sQuery(id+"F18.wireOp",EDGE,"E114.MirrorCS"),sQuery(id+"F18.wireOp",EDGE,"E115.MirrorCS"),sQuery(id+"F18.wireOp",EDGE,"E116.MirrorCS"),sQuery(id+"F18.wireOp",EDGE,"E117.MirrorCS"),sQuery(id+"F18.wireOp",EDGE,"E118.MirrorCS"),sQuery(id+"F18.wireOp",EDGE,"E119.MirrorCS"),sQuery(id+"F18.wireOp",EDGE,"E120.MirrorCS"),sQuery(id+"F18.wireOp",EDGE,"E121.MirrorCS"),sQuery(id+"F18.wireOp",EDGE,"E122.MirrorCS"),sQuery(id+"F18.wireOp",EDGE,"E123.MirrorCS"),sQuery(id+"F18.wireOp",EDGE,"E124.MirrorCS"),sQuery(id+"F18.wireOp",EDGE,"E125.MirrorCS"),sQuery(id+"F18.wireOp",EDGE,"E126.MirrorCS"),sQuery(id+"F18.wireOp",EDGE,"E127.MirrorCS"),sQuery(id+"F18.wireOp",EDGE,"E128.MirrorCS"),sQuery(id+"F18.wireOp",EDGE,"E129.MirrorCS"),sQuery(id+"F18.wireOp",EDGE,"E130.MirrorCS"),sQuery(id+"F18.wireOp",EDGE,"E131.MirrorCS"),sQuery(id+"F18.wireOp",EDGE,"E132.MirrorCS"),sQuery(id+"F18.wireOp",EDGE,"E133.MirrorCS"),sQuery(id+"F18.wireOp",EDGE,"E134.MirrorCS"),sQuery(id+"F18.wireOp",EDGE,"E135.MirrorCS"),sQuery(id+"F18.wireOp",EDGE,"E136.MirrorCS"),sQuery(id+"F18.wireOp",EDGE,"E137.MirrorCS"),sQuery(id+"F18.wireOp",EDGE,"E138.MirrorCS"),sQuery(id+"F18.wireOp",EDGE,"E139.MirrorCS"),sQuery(id+"F18.wireOp",EDGE,"E140.MirrorCS"),sQuery(id+"F18.wireOp",EDGE,"E141.MirrorCS"),sQuery(id+"F18.wireOp",EDGE,"E142.MirrorCS"),sQuery(id+"F18.wireOp",EDGE,"E143.MirrorCS"),sQuery(id+"F18.wireOp",EDGE,"E144.MirrorCS"),sQuery(id+"F18.wireOp",EDGE,"E145.MirrorCS"),sQuery(id+"F18.wireOp",EDGE,"E146.MirrorCS"),sQuery(id+"F18.wireOp",EDGE,"E147.MirrorCS"),sQuery(id+"F18.wireOp",EDGE,"E148.MirrorCS"),sQuery(id+"F18.wireOp",EDGE,"E149.MirrorCS"),sQuery(id+"F18.wireOp",EDGE,"E150.MirrorCS"),sQuery(id+"F18.wireOp",EDGE,"E151.MirrorCS"),sQuery(id+"F18.wireOp",EDGE,"E152.MirrorCS"),sQuery(id+"F18.wireOp",EDGE,"E153.trimOffspring"),sQuery(id+"F18.wireOp",EDGE,"E154.trimOffspring"),sQuery(id+"F18.wireOp",EDGE,"E155.trimOffspring"),sQuery(id+"F18.wireOp",EDGE,"E156.trimOffspring"),sQuery(id+"F18.wireOp",EDGE,"E157.trimOffspring"),sQuery(id+"F18.wireOp",EDGE,"E158.trimOffspring"),sQuery(id+"F18.wireOp",EDGE,"E159.trimOffspring"),sQuery(id+"F18.wireOp",EDGE,"E160.trimOffspring"),sQuery(id+"F18.wireOp",EDGE,"E161.trimOffspring"),sQuery(id+"F18.wireOp",EDGE,"E162.trimOffspring"),sQuery(id+"F18.wireOp",EDGE,"E163.trimOffspring"),sQuery(id+"F18.wireOp",EDGE,"E164.trimOffspring"),sQuery(id+"F18.wireOp",EDGE,"E165.trimOffspring"),sQuery(id+"F18.wireOp",EDGE,"E166.trimOffspring"),sQuery(id+"F18.wireOp",EDGE,"E167.trimOffspring"),sQuery(id+"F18.wireOp",EDGE,"E168.trimOffspring"),sQuery(id+"F18.wireOp",EDGE,"E169.trimOffspring"),sQuery(id+"F18.wireOp",EDGE,"E170.trimOffspring"),sQuery(id+"F18.wireOp",EDGE,"E171.0"),sQuery(id+"F18.wireOp",EDGE,"E172.0"),sQuery(id+"F18.wireOp",EDGE,"E173.0"),sQuery(id+"F18.wireOp",EDGE,"E174.0"),sQuery(id+"F18.wireOp",EDGE,"E175.0"),sQuery(id+"F18.wireOp",EDGE,"E176.0"),sQuery(id+"F18.wireOp",EDGE,"E177.0"),sQuery(id+"F18.wireOp",EDGE,"E178.0"),sQuery(id+"F18.wireOp",EDGE,"E179.0"),sQuery(id+"F18.wireOp",EDGE,"E180.0"),sQuery(id+"F18.wireOp",EDGE,"E181.0"),sQuery(id+"F18.wireOp",EDGE,"E182.0"),sQuery(id+"F18.wireOp",EDGE,"E183.trimOffspring"),sQuery(id+"F18.wireOp",EDGE,"E184.0"),sQuery(id+"F18.wireOp",EDGE,"E185.0"),sQuery(id+"F18.wireOp",EDGE,"E186.0"),sQuery(id+"F18.wireOp",EDGE,"E187.0"),sQuery(id+"F18.wireOp",EDGE,"E188.0"),sQuery(id+"F18.wireOp",EDGE,"E189.0"),sQuery(id+"F18.wireOp",EDGE,"E190.trimOffspring"),sQuery(id+"F18.wireOp",EDGE,"E191.0"),sQuery(id+"F18.wireOp",EDGE,"E192.0"),sQuery(id+"F18.wireOp",EDGE,"E193.0"),sQuery(id+"F18.wireOp",EDGE,"E194.0"),sQuery(id+"F18.wireOp",EDGE,"E195.0"),sQuery(id+"F18.wireOp",EDGE,"E196.0"),sQuery(id+"F18.wireOp",EDGE,"E197.0"),sQuery(id+"F18.wireOp",EDGE,"E198.0"),sQuery(id+"F18.wireOp",EDGE,"E199.0"),sQuery(id+"F18.wireOp",EDGE,"E200.0"),sQuery(id+"F18.wireOp",EDGE,"E201.0"),sQuery(id+"F18.wireOp",EDGE,"E202.0"),sQuery(id+"F18.wireOp",EDGE,"E203.trimOffspring"),sQuery(id+"F18.wireOp",EDGE,"E204.trimOffspring"),sQuery(id+"F18.wireOp",EDGE,"E205.trimOffspring"),sQuery(id+"F18.wireOp",EDGE,"E206.0"),sQuery(id+"F18.wireOp",EDGE,"E207.0"),sQuery(id+"F18.wireOp",EDGE,"E208.0"),sQuery(id+"F18.wireOp",EDGE,"E209.0"),sQuery(id+"F18.wireOp",EDGE,"E210.0"),sQuery(id+"F18.wireOp",EDGE,"E211.trimOffspring"),sQuery(id+"F18.wireOp",EDGE,"E212.0"),sQuery(id+"F18.wireOp",EDGE,"E213.MirrorCS"),sQuery(id+"F18.wireOp",EDGE,"E214.MirrorCS"),sQuery(id+"F18.wireOp",EDGE,"E215.MirrorCS"),sQuery(id+"F18.wireOp",EDGE,"E216.MirrorCS"),sQuery(id+"F18.wireOp",EDGE,"E217.MirrorCS"),sQuery(id+"F18.wireOp",EDGE,"E218.MirrorCS"),sQuery(id+"F18.wireOp",EDGE,"E219.MirrorCS"),sQuery(id+"F18.wireOp",EDGE,"E220.MirrorCS"),sQuery(id+"F18.wireOp",EDGE,"E221.MirrorCS"),sQuery(id+"F18.wireOp",EDGE,"E222.MirrorCS"),sQuery(id+"F18.wireOp",EDGE,"E223.MirrorCS"),sQuery(id+"F18.wireOp",EDGE,"E224.MirrorCS"),sQuery(id+"F18.wireOp",EDGE,"E225.MirrorCS"),sQuery(id+"F18.wireOp",EDGE,"E226.MirrorCS"),sQuery(id+"F18.wireOp",EDGE,"E227.MirrorCS"),sQuery(id+"F18.wireOp",EDGE,"E228.MirrorCS"),sQuery(id+"F18.wireOp",EDGE,"E229.MirrorCS"),sQuery(id+"F18.wireOp",EDGE,"E230.MirrorCS"),sQuery(id+"F18.wireOp",EDGE,"E231.MirrorCS"),sQuery(id+"F18.wireOp",EDGE,"E232.MirrorCS"),sQuery(id+"F18.wireOp",EDGE,"E233.MirrorCS"),sQuery(id+"F18.wireOp",EDGE,"E234.MirrorCS"),sQuery(id+"F18.wireOp",EDGE,"E235.MirrorCS"),sQuery(id+"F18.wireOp",EDGE,"E236.MirrorCS"),sQuery(id+"F18.wireOp",EDGE,"E237.MirrorCS"),sQuery(id+"F18.wireOp",EDGE,"E238.MirrorCS"),sQuery(id+"F18.wireOp",EDGE,"E239.MirrorCS"),sQuery(id+"F18.wireOp",EDGE,"E240.MirrorCS"),sQuery(id+"F18.wireOp",EDGE,"E241.MirrorCS"),sQuery(id+"F18.wireOp",EDGE,"E242.MirrorCS"),sQuery(id+"F18.wireOp",EDGE,"E243.MirrorCS"),sQuery(id+"F18.wireOp",EDGE,"E244.MirrorCS"),sQuery(id+"F18.wireOp",EDGE,"E245.MirrorCS"),sQuery(id+"F18.wireOp",EDGE,"E246.MirrorCS"),sQuery(id+"F18.wireOp",EDGE,"E247.MirrorCS"),sQuery(id+"F18.wireOp",EDGE,"E248.MirrorCS"),sQuery(id+"F18.wireOp",EDGE,"E249.MirrorCS"),sQuery(id+"F18.wireOp",EDGE,"E250.MirrorCS"),sQuery(id+"F18.wireOp",EDGE,"E251.MirrorCS"),sQuery(id+"F18.wireOp",EDGE,"E252.MirrorCS"),sQuery(id+"F18.wireOp",EDGE,"E253"),sQuery(id+"F18.wireOp",EDGE,"E254"),sQuery(id+"F18.wireOp",EDGE,"E255"),sQuery(id+"F18.wireOp",EDGE,"E256")])],"isStart":false})});
            var sketch = newSketch(context, id + "F22", { "sketchPlane" : qUnion([Q0])});
            skLineSegment(sketch, "E336.0", {"start": v(35, -14.44) * mm, "end": v(35, -14.42) * mm});
            skArc(sketch, "E337.0", {"start": v(35, -14.42) * mm, "mid": v(34.8, -14.4) * mm, "end": v(34.6, -14.4) * mm});
            skArc(sketch, "E337.1", {"start": v(35, -14.44) * mm, "mid": v(31.87, -18.77) * mm, "end": v(27.07, -21.11) * mm});
            skArc(sketch, "E338", {"start": v(27.07, -21.11) * mm, "mid": v(31.72, -18.76) * mm, "end": v(34.6, -14.4) * mm});
            skPoint(sketch, "E339.orphan", {"position": v(29.72, -15.45) * mm});
            skArc(sketch, "E340.MirrorCS", {"start": v(-35, -14.44) * mm, "mid": v(-31.87, -18.77) * mm, "end": v(-27.07, -21.11) * mm});
            skArc(sketch, "E341.MirrorCS", {"start": v(-35, -14.42) * mm, "mid": v(-34.8, -14.4) * mm, "end": v(-34.6, -14.4) * mm});
            skArc(sketch, "E342.MirrorCS", {"start": v(-27.07, -21.11) * mm, "mid": v(-31.72, -18.76) * mm, "end": v(-34.6, -14.4) * mm});
            skSolve(sketch);
        }
        {
            var Q0;
            Q0 = qSketchRegion(id + "F22", true);
            var Q1;
            Q1=makeQuery(id+"F22.imprint","IMPRINT",FACE,{"disambiguationData":[TD([[makeQuery(id+"F22.imprint","IMPRINT",EDGE,{"derivedFrom":sQuery(id+"F22.wireOp",EDGE,"E340.MirrorCS")}),1.0]])]});
            var Q2;
            {var subQ1=sQuery(id+"F0.wireOp",EDGE,"E0.left");var subQ3=sQuery(id+"F0.wireOp",EDGE,"E0.right");Q2=makeQuery(id+"F19.boolean.opBoolean","SPLIT",FACE,{"disambiguationData":[TD([makeQuery(id+"F3.boolean.opBoolean","COPY",FACE,{"derivedFrom":makeQuery(id+"F3.opExtrude","SWEPT_FACE",FACE,{"disambiguationData":[OSD([sQuery(id+"F2.wireOp",EDGE,"E1.top")])]})})])],"derivedFrom":makeQuery(id+"F1.opExtrude","CAP_FACE",FACE,{"disambiguationData":[OSD([sQuery(id+"F0.wireOp",EDGE,"E0.bottom"),sQuery(id+"F0.wireOp",EDGE,"E0.top"),subQ1,subQ3])],"isStart":false})});}
            extrude(context, id + "F23", {"entities" : qUnion([Q0, Q1]), "operationType" : NewBodyOperationType.ADD, "endBound" : BoundingType.UP_TO_SURFACE, "endBoundEntityFace" : qUnion([Q2]), "depth" : 25 * mm});
        }
        {
            var Q0;
            Q0=makeQuery(id+"F21.boolean.opBoolean","COPY",EDGE,{"derivedFrom":makeQuery(id+"F21.opExtrude","SWEPT_EDGE",EDGE,{"disambiguationData":[OSD([sQuery(id+"F20.wireOp",EDGE,"E313"),sQuery(id+"F20.wireOp",EDGE,"E314")])]})});
            var Q1;
            Q1=makeQuery(id+"F21.boolean.opBoolean","COPY",EDGE,{"derivedFrom":makeQuery(id+"F21.opExtrude","SWEPT_EDGE",EDGE,{"disambiguationData":[OSD([sQuery(id+"F20.wireOp",EDGE,"E307"),sQuery(id+"F20.wireOp",EDGE,"E327.trimOffspring")])]})});
            var Q2;
            Q2=makeQuery(id+"F21.boolean.opBoolean","COPY",EDGE,{"derivedFrom":makeQuery(id+"F21.opExtrude","SWEPT_EDGE",EDGE,{"disambiguationData":[OSD([sQuery(id+"F20.wireOp",EDGE,"E311"),sQuery(id+"F20.wireOp",EDGE,"E327.trimOffspring")])]})});
            var Q3;
            Q3=makeQuery(id+"F21.boolean.opBoolean","COPY",EDGE,{"derivedFrom":makeQuery(id+"F21.opExtrude","SWEPT_EDGE",EDGE,{"disambiguationData":[OSD([sQuery(id+"F20.wireOp",EDGE,"E311"),sQuery(id+"F20.wireOp",EDGE,"E314")])]})});
            var Q4;
            Q4=makeQuery(id+"F21.boolean.opBoolean","COPY",EDGE,{"derivedFrom":makeQuery(id+"F21.opExtrude","SWEPT_EDGE",EDGE,{"disambiguationData":[OSD([sQuery(id+"F20.wireOp",EDGE,"E312"),sQuery(id+"F20.wireOp",EDGE,"E313")])]})});
            var Q5;
            Q5=makeQuery(id+"F21.boolean.opBoolean","COPY",EDGE,{"derivedFrom":makeQuery(id+"F21.opExtrude","SWEPT_EDGE",EDGE,{"disambiguationData":[OSD([sQuery(id+"F20.wireOp",EDGE,"E309"),sQuery(id+"F20.wireOp",EDGE,"E312")])]})});
            var Q6;
            Q6=makeQuery(id+"F21.boolean.opBoolean","COPY",EDGE,{"derivedFrom":makeQuery(id+"F21.opExtrude","SWEPT_EDGE",EDGE,{"disambiguationData":[OSD([sQuery(id+"F20.wireOp",EDGE,"E291.0"),sQuery(id+"F20.wireOp",EDGE,"E307")])]})});
            var Q7;
            Q7=makeQuery(id+"F21.boolean.opBoolean","COPY",EDGE,{"derivedFrom":makeQuery(id+"F21.opExtrude","SWEPT_EDGE",EDGE,{"disambiguationData":[OSD([sQuery(id+"F20.wireOp",EDGE,"E272.0"),sQuery(id+"F20.wireOp",EDGE,"E278")])]})});
            var Q8;
            Q8=makeQuery(id+"F21.boolean.opBoolean","COPY",EDGE,{"derivedFrom":makeQuery(id+"F21.opExtrude","SWEPT_EDGE",EDGE,{"disambiguationData":[OSD([sQuery(id+"F20.wireOp",EDGE,"E271.0"),sQuery(id+"F20.wireOp",EDGE,"E272.0")])]})});
            var Q9;
            Q9=makeQuery(id+"F21.boolean.opBoolean","COPY",EDGE,{"derivedFrom":makeQuery(id+"F21.opExtrude","SWEPT_EDGE",EDGE,{"disambiguationData":[OSD([sQuery(id+"F20.wireOp",EDGE,"E279"),sQuery(id+"F20.wireOp",EDGE,"E281")])]})});
            var Q10;
            Q10=makeQuery(id+"F21.boolean.opBoolean","COPY",EDGE,{"derivedFrom":makeQuery(id+"F21.opExtrude","SWEPT_EDGE",EDGE,{"disambiguationData":[OSD([sQuery(id+"F20.wireOp",EDGE,"E274.0"),sQuery(id+"F20.wireOp",EDGE,"E275.0")])]})});
            var Q11;
            Q11=makeQuery(id+"F21.boolean.opBoolean","COPY",EDGE,{"derivedFrom":makeQuery(id+"F21.opExtrude","SWEPT_EDGE",EDGE,{"disambiguationData":[OSD([sQuery(id+"F20.wireOp",EDGE,"E275.0"),sQuery(id+"F20.wireOp",EDGE,"E276.0")])]})});
            var Q12;
            Q12=makeQuery(id+"F21.boolean.opBoolean","COPY",EDGE,{"derivedFrom":makeQuery(id+"F21.opExtrude","SWEPT_EDGE",EDGE,{"disambiguationData":[OSD([sQuery(id+"F20.wireOp",EDGE,"E276.0"),sQuery(id+"F20.wireOp",EDGE,"E277.0")])]})});
            var Q13;
            Q13=makeQuery(id+"F21.boolean.opBoolean","COPY",EDGE,{"derivedFrom":makeQuery(id+"F21.opExtrude","SWEPT_EDGE",EDGE,{"disambiguationData":[OSD([sQuery(id+"F20.wireOp",EDGE,"E271.0"),sQuery(id+"F20.wireOp",EDGE,"E277.0")])]})});
            var Q14;
            Q14=makeQuery(id+"F21.boolean.opBoolean","COPY",EDGE,{"derivedFrom":makeQuery(id+"F21.opExtrude","SWEPT_EDGE",EDGE,{"disambiguationData":[OSD([sQuery(id+"F20.wireOp",EDGE,"E263"),sQuery(id+"F20.wireOp",EDGE,"E264")])]})});
            var Q15;
            Q15=makeQuery(id+"F21.boolean.opBoolean","COPY",EDGE,{"derivedFrom":makeQuery(id+"F21.opExtrude","SWEPT_EDGE",EDGE,{"disambiguationData":[OSD([sQuery(id+"F20.wireOp",EDGE,"E262"),sQuery(id+"F20.wireOp",EDGE,"E263")])]})});
            var Q16;
            Q16=makeQuery(id+"F21.boolean.opBoolean","COPY",EDGE,{"derivedFrom":makeQuery(id+"F21.opExtrude","SWEPT_EDGE",EDGE,{"disambiguationData":[OSD([sQuery(id+"F20.wireOp",EDGE,"E264"),sQuery(id+"F20.wireOp",EDGE,"E265")])]})});
            var Q17;
            Q17=makeQuery(id+"F21.boolean.opBoolean","COPY",EDGE,{"derivedFrom":makeQuery(id+"F21.opExtrude","SWEPT_EDGE",EDGE,{"disambiguationData":[OSD([sQuery(id+"F20.wireOp",EDGE,"E265"),sQuery(id+"F20.wireOp",EDGE,"E266")])]})});
            var Q18;
            Q18=makeQuery(id+"F21.boolean.opBoolean","COPY",EDGE,{"derivedFrom":makeQuery(id+"F21.opExtrude","SWEPT_EDGE",EDGE,{"disambiguationData":[OSD([sQuery(id+"F20.wireOp",EDGE,"E266"),sQuery(id+"F20.wireOp",EDGE,"E269")])]})});
            var Q19;
            Q19=makeQuery(id+"F21.boolean.opBoolean","COPY",EDGE,{"derivedFrom":makeQuery(id+"F21.opExtrude","SWEPT_EDGE",EDGE,{"disambiguationData":[OSD([sQuery(id+"F20.wireOp",EDGE,"E261"),sQuery(id+"F20.wireOp",EDGE,"E269")])]})});
            var Q20;
            Q20=makeQuery(id+"F21.boolean.opBoolean","COPY",EDGE,{"derivedFrom":makeQuery(id+"F21.opExtrude","SWEPT_EDGE",EDGE,{"disambiguationData":[OSD([sQuery(id+"F20.wireOp",EDGE,"E261"),sQuery(id+"F20.wireOp",EDGE,"E262")])]})});
            fillet(context, id + "F24", {"entities" : qUnion([Q0, Q1, Q2, Q3, Q4, Q5, Q6, Q7, Q8, Q9, Q10, Q11, Q12, Q13, Q14, Q15, Q16, Q17, Q18, Q19, Q20]), "radius" : 1 * mm, "tangentPropagation" : true, "allowEdgeOverflow" : false});
        }
        {
            var Q0;
            Q0=makeQuery(id+"F21.boolean.opBoolean","COPY",EDGE,{"derivedFrom":makeQuery(id+"F21.opExtrude","SWEPT_EDGE",EDGE,{"disambiguationData":[OSD([sQuery(id+"F20.wireOp",EDGE,"E302.bottom"),sQuery(id+"F20.wireOp",EDGE,"E302.left")])]})});
            var Q1;
            Q1=makeQuery(id+"F21.boolean.opBoolean","COPY",EDGE,{"derivedFrom":makeQuery(id+"F21.opExtrude","SWEPT_EDGE",EDGE,{"disambiguationData":[OSD([sQuery(id+"F20.wireOp",EDGE,"E301.left"),sQuery(id+"F20.wireOp",EDGE,"E302.bottom")])]})});
            var Q2;
            Q2=makeQuery(id+"F21.boolean.opBoolean","COPY",EDGE,{"derivedFrom":makeQuery(id+"F21.opExtrude","SWEPT_EDGE",EDGE,{"disambiguationData":[OSD([sQuery(id+"F20.wireOp",EDGE,"E301.bottom"),sQuery(id+"F20.wireOp",EDGE,"E301.left")])]})});
            var Q3;
            Q3=makeQuery(id+"F21.boolean.opBoolean","COPY",EDGE,{"derivedFrom":makeQuery(id+"F21.opExtrude","SWEPT_EDGE",EDGE,{"disambiguationData":[OSD([sQuery(id+"F20.wireOp",EDGE,"E301.bottom"),sQuery(id+"F20.wireOp",EDGE,"E301.right")])]})});
            var Q4;
            Q4=makeQuery(id+"F21.boolean.opBoolean","COPY",EDGE,{"derivedFrom":makeQuery(id+"F21.opExtrude","SWEPT_EDGE",EDGE,{"disambiguationData":[OSD([sQuery(id+"F20.wireOp",EDGE,"E304.trimOffspring"),sQuery(id+"F20.wireOp",EDGE,"E325.trimOffspring")])]})});
            var Q5;
            Q5=makeQuery(id+"F21.boolean.opBoolean","COPY",EDGE,{"derivedFrom":makeQuery(id+"F21.opExtrude","SWEPT_EDGE",EDGE,{"disambiguationData":[OSD([sQuery(id+"F20.wireOp",EDGE,"E332"),sQuery(id+"F20.wireOp",EDGE,"E333")])]})});
            var Q6;
            Q6=makeQuery(id+"F21.boolean.opBoolean","COPY",EDGE,{"derivedFrom":makeQuery(id+"F21.opExtrude","SWEPT_EDGE",EDGE,{"disambiguationData":[OSD([sQuery(id+"F20.wireOp",EDGE,"E301.top"),sQuery(id+"F20.wireOp",EDGE,"E303.trimOffspring")])]})});
            var Q7;
            Q7=makeQuery(id+"F21.boolean.opBoolean","COPY",EDGE,{"derivedFrom":makeQuery(id+"F21.opExtrude","SWEPT_EDGE",EDGE,{"disambiguationData":[OSD([sQuery(id+"F20.wireOp",EDGE,"E302.top"),sQuery(id+"F20.wireOp",EDGE,"E302.left")])]})});
            var Q8;
            Q8=makeQuery(id+"F21.boolean.opBoolean","COPY",EDGE,{"derivedFrom":makeQuery(id+"F21.opExtrude","SWEPT_EDGE",EDGE,{"disambiguationData":[OSD([sQuery(id+"F20.wireOp",EDGE,"E302.top"),sQuery(id+"F20.wireOp",EDGE,"E303.trimOffspring")])]})});
            var Q9;
            Q9=makeQuery(id+"F21.boolean.opBoolean","COPY",EDGE,{"derivedFrom":makeQuery(id+"F21.opExtrude","SWEPT_EDGE",EDGE,{"disambiguationData":[OSD([sQuery(id+"F20.wireOp",EDGE,"E305.trimOffspring"),sQuery(id+"F20.wireOp",EDGE,"E325.trimOffspring")])]})});
            var Q10;
            Q10=makeQuery(id+"F21.boolean.opBoolean","COPY",EDGE,{"derivedFrom":makeQuery(id+"F21.opExtrude","SWEPT_EDGE",EDGE,{"disambiguationData":[OSD([sQuery(id+"F20.wireOp",EDGE,"E331"),sQuery(id+"F20.wireOp",EDGE,"E332")])]})});
            var Q11;
            Q11=makeQuery(id+"F21.boolean.opBoolean","COPY",EDGE,{"derivedFrom":makeQuery(id+"F21.opExtrude","SWEPT_EDGE",EDGE,{"disambiguationData":[OSD([sQuery(id+"F20.wireOp",EDGE,"E305.trimOffspring"),sQuery(id+"F20.wireOp",EDGE,"E306.trimOffspring")])]})});
            var Q12;
            Q12=makeQuery(id+"F21.boolean.opBoolean","COPY",EDGE,{"derivedFrom":makeQuery(id+"F21.opExtrude","SWEPT_EDGE",EDGE,{"disambiguationData":[OSD([sQuery(id+"F20.wireOp",EDGE,"E317"),sQuery(id+"F20.wireOp",EDGE,"E324")])]})});
            var Q13;
            Q13=makeQuery(id+"F21.boolean.opBoolean","COPY",EDGE,{"derivedFrom":makeQuery(id+"F21.opExtrude","SWEPT_EDGE",EDGE,{"disambiguationData":[OSD([sQuery(id+"F20.wireOp",EDGE,"E316"),sQuery(id+"F20.wireOp",EDGE,"E317")])]})});
            var Q14;
            Q14=makeQuery(id+"F21.boolean.opBoolean","COPY",EDGE,{"derivedFrom":makeQuery(id+"F21.opExtrude","SWEPT_EDGE",EDGE,{"disambiguationData":[OSD([sQuery(id+"F20.wireOp",EDGE,"E315"),sQuery(id+"F20.wireOp",EDGE,"E316")])]})});
            var Q15;
            Q15=makeQuery(id+"F21.boolean.opBoolean","COPY",EDGE,{"derivedFrom":makeQuery(id+"F21.opExtrude","SWEPT_EDGE",EDGE,{"disambiguationData":[OSD([sQuery(id+"F20.wireOp",EDGE,"E322"),sQuery(id+"F20.wireOp",EDGE,"E323")])]})});
            var Q16;
            Q16=makeQuery(id+"F21.boolean.opBoolean","COPY",EDGE,{"derivedFrom":makeQuery(id+"F21.opExtrude","SWEPT_EDGE",EDGE,{"disambiguationData":[OSD([sQuery(id+"F20.wireOp",EDGE,"E321"),sQuery(id+"F20.wireOp",EDGE,"E322")])]})});
            var Q17;
            Q17=makeQuery(id+"F21.boolean.opBoolean","COPY",EDGE,{"derivedFrom":makeQuery(id+"F21.opExtrude","SWEPT_EDGE",EDGE,{"disambiguationData":[OSD([sQuery(id+"F20.wireOp",EDGE,"E320"),sQuery(id+"F20.wireOp",EDGE,"E321")])]})});
            var Q18;
            Q18=makeQuery(id+"F21.boolean.opBoolean","COPY",EDGE,{"derivedFrom":makeQuery(id+"F21.opExtrude","SWEPT_EDGE",EDGE,{"disambiguationData":[OSD([sQuery(id+"F20.wireOp",EDGE,"E318"),sQuery(id+"F20.wireOp",EDGE,"E319")])]})});
            var Q19;
            Q19=makeQuery(id+"F21.boolean.opBoolean","COPY",EDGE,{"derivedFrom":makeQuery(id+"F21.opExtrude","SWEPT_EDGE",EDGE,{"disambiguationData":[OSD([sQuery(id+"F20.wireOp",EDGE,"E323"),sQuery(id+"F20.wireOp",EDGE,"E324")])]})});
            var Q20;
            Q20=makeQuery(id+"F21.boolean.opBoolean","COPY",EDGE,{"derivedFrom":makeQuery(id+"F21.opExtrude","SWEPT_EDGE",EDGE,{"disambiguationData":[OSD([sQuery(id+"F20.wireOp",EDGE,"E319"),sQuery(id+"F20.wireOp",EDGE,"E320")])]})});
            var Q21;
            Q21=makeQuery(id+"F21.boolean.opBoolean","COPY",EDGE,{"derivedFrom":makeQuery(id+"F21.opExtrude","SWEPT_EDGE",EDGE,{"disambiguationData":[OSD([sQuery(id+"F20.wireOp",EDGE,"E315"),sQuery(id+"F20.wireOp",EDGE,"E318")])]})});
            fillet(context, id + "F25", {"entities" : qUnion([Q0, Q1, Q2, Q3, Q4, Q5, Q6, Q7, Q8, Q9, Q10, Q11, Q12, Q13, Q14, Q15, Q16, Q17, Q18, Q19, Q20, Q21]), "radius" : 0.5 * mm, "tangentPropagation" : true, "allowEdgeOverflow" : false});
        }
    });
